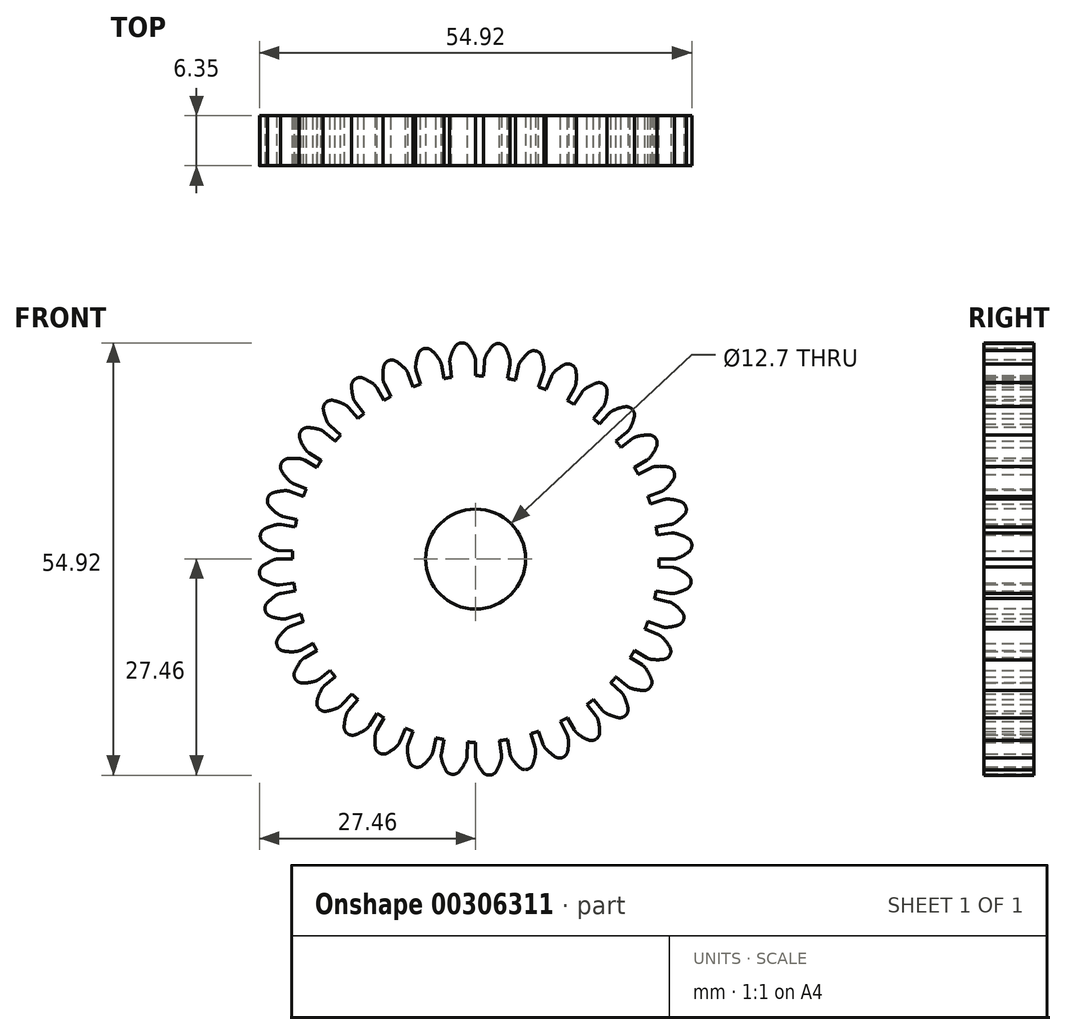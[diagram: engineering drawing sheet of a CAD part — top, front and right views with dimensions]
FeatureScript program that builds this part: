
annotation { "Feature Type Name" : "Feature", "Feature Type Description" : "" }
export const myFeature = defineFeature(function(context is Context, id is Id, definition is map)
    precondition{}
    {
        {
            var Q0;
            Q0=qCreatedBy(makeId("Front.planeOp"),FACE);
            var sketch = newSketch(context, id + "F0", { "sketchPlane" : qUnion([Q0])});
            skCircle(sketch, "E0", {"center": v(0, 0) * mm, "radius": 23.28 * mm});
            skArc(sketch, "E1.trimOffspring", {"start": v(-0.13, 25.73) * mm, "mid": v(-0.47, 26.41) * mm, "end": v(-0.9, 27.06) * mm});
            skLineSegment(sketch, "E2", {"start": v(0, 25.1) * mm, "end": v(0, 23.28) * mm});
            skLineSegment(sketch, "E3", {"start": v(-1.78, 27.46) * mm, "end": v(-1.8, 27.46) * mm});
            skArc(sketch, "E4.MirrorCS", {"start": v(-3.23, 25.52) * mm, "mid": v(-2.98, 26.25) * mm, "end": v(-2.64, 26.94) * mm});
            skLineSegment(sketch, "E5.MirrorCS", {"start": v(-3.28, 24.88) * mm, "end": v(-3.04, 23.08) * mm});
            skLineSegment(sketch, "E6.MirrorCS", {"start": v(-1.82, 27.46) * mm, "end": v(-1.8, 27.46) * mm});
            skPoint(sketch, "E7.visualSharp", {"position": v(-1.26, 27.5) * mm});
            skArc(sketch, "E7.filletArc", {"start": v(-0.9, 27.06) * mm, "mid": v(-1.29, 27.37) * mm, "end": v(-1.78, 27.46) * mm});
            skPoint(sketch, "E8.visualSharp", {"position": v(-2.34, 27.42) * mm});
            skArc(sketch, "E8.filletArc", {"start": v(-1.82, 27.46) * mm, "mid": v(-2.3, 27.3) * mm, "end": v(-2.64, 26.94) * mm});
            skPoint(sketch, "E9.visualSharp", {"position": v(-3.32, 25.18) * mm});
            skArc(sketch, "E9.filletArc", {"start": v(-3.27, 25.38) * mm, "mid": v(-3.3, 25.2) * mm, "end": v(-3.3, 25) * mm});
            skArc(sketch, "E10.filletArc", {"start": v(-3.23, 25.52) * mm, "mid": v(-3.29, 25.2) * mm, "end": v(-3.28, 24.88) * mm});
            skPoint(sketch, "E11.visualSharp", {"position": v(0, 25.4) * mm});
            skArc(sketch, "E11.filletArc", {"start": v(0, 25.1) * mm, "mid": v(-0.03, 25.42) * mm, "end": v(-0.13, 25.73) * mm});
            skArc(sketch, "E12.1.0", {"start": v(-5.59, 26.49) * mm, "mid": v(-6.02, 26.73) * mm, "end": v(-6.52, 26.73) * mm});
            skArc(sketch, "E12.1.1", {"start": v(-6.56, 26.72) * mm, "mid": v(-7, 26.49) * mm, "end": v(-7.28, 26.08) * mm});
            skArc(sketch, "E12.1.2", {"start": v(-7.61, 24.57) * mm, "mid": v(-7.5, 25.34) * mm, "end": v(-7.28, 26.08) * mm});
            skArc(sketch, "E12.1.3", {"start": v(-7.61, 24.57) * mm, "mid": v(-7.61, 24.25) * mm, "end": v(-7.55, 23.94) * mm});
            skLineSegment(sketch, "E12.1.4", {"start": v(-7.55, 23.94) * mm, "end": v(-7, 22.2) * mm});
            skLineSegment(sketch, "E12.1.5", {"start": v(-4.36, 24.72) * mm, "end": v(-4.04, 22.93) * mm});
            skArc(sketch, "E12.1.6", {"start": v(-4.36, 24.72) * mm, "mid": v(-4.45, 25.03) * mm, "end": v(-4.6, 25.31) * mm});
            skArc(sketch, "E12.1.7", {"start": v(-4.6, 25.31) * mm, "mid": v(-5.05, 25.93) * mm, "end": v(-5.59, 26.49) * mm});
            skArc(sketch, "E12.2.0", {"start": v(-10.1, 25.12) * mm, "mid": v(-10.57, 25.28) * mm, "end": v(-11.06, 25.2) * mm});
            skArc(sketch, "E12.2.1", {"start": v(-11.1, 25.18) * mm, "mid": v(-11.5, 24.87) * mm, "end": v(-11.7, 24.42) * mm});
            skArc(sketch, "E12.2.2", {"start": v(-11.76, 22.88) * mm, "mid": v(-11.78, 23.65) * mm, "end": v(-11.7, 24.42) * mm});
            skArc(sketch, "E12.2.3", {"start": v(-11.76, 22.88) * mm, "mid": v(-11.7, 22.56) * mm, "end": v(-11.59, 22.26) * mm});
            skLineSegment(sketch, "E12.2.4", {"start": v(-11.59, 22.26) * mm, "end": v(-10.75, 20.65) * mm});
            skLineSegment(sketch, "E12.2.5", {"start": v(-8.58, 23.58) * mm, "end": v(-7.96, 21.88) * mm});
            skArc(sketch, "E12.2.6", {"start": v(-8.58, 23.58) * mm, "mid": v(-8.72, 23.87) * mm, "end": v(-8.92, 24.13) * mm});
            skArc(sketch, "E12.2.7", {"start": v(-8.92, 24.13) * mm, "mid": v(-9.48, 24.66) * mm, "end": v(-10.1, 25.12) * mm});
            skArc(sketch, "E13.1.3.0", {"start": v(-14.3, 22.98) * mm, "mid": v(-14.8, 23.06) * mm, "end": v(-15.27, 22.9) * mm});
            skArc(sketch, "E13.4.3.0", {"start": v(-15.3, 22.87) * mm, "mid": v(-15.64, 22.5) * mm, "end": v(-15.76, 22.01) * mm});
            skArc(sketch, "E13.8.3.0", {"start": v(-15.56, 20.49) * mm, "mid": v(-15.7, 21.25) * mm, "end": v(-15.76, 22.01) * mm});
            skArc(sketch, "E13.12.3.0", {"start": v(-15.56, 20.49) * mm, "mid": v(-15.45, 20.19) * mm, "end": v(-15.28, 19.91) * mm});
            skLineSegment(sketch, "E13.16.3.0", {"start": v(-15.28, 19.91) * mm, "end": v(-14.17, 18.47) * mm});
            skLineSegment(sketch, "E13.19.3.0", {"start": v(-12.55, 21.73) * mm, "end": v(-11.64, 20.16) * mm});
            skArc(sketch, "E13.22.3.0", {"start": v(-12.55, 21.73) * mm, "mid": v(-12.74, 22) * mm, "end": v(-12.97, 22.21) * mm});
            skArc(sketch, "E13.26.3.0", {"start": v(-12.97, 22.21) * mm, "mid": v(-13.62, 22.64) * mm, "end": v(-14.3, 22.98) * mm});
            skArc(sketch, "E13.1.4.0", {"start": v(-18.08, 20.15) * mm, "mid": v(-18.58, 20.14) * mm, "end": v(-19.01, 19.9) * mm});
            skArc(sketch, "E13.4.4.0", {"start": v(-19.04, 19.86) * mm, "mid": v(-19.3, 19.44) * mm, "end": v(-19.34, 18.94) * mm});
            skArc(sketch, "E13.8.4.0", {"start": v(-18.88, 17.48) * mm, "mid": v(-19.15, 18.2) * mm, "end": v(-19.34, 18.94) * mm});
            skArc(sketch, "E13.12.4.0", {"start": v(-18.88, 17.48) * mm, "mid": v(-18.72, 17.2) * mm, "end": v(-18.5, 16.96) * mm});
            skLineSegment(sketch, "E13.16.4.0", {"start": v(-18.5, 16.96) * mm, "end": v(-17.16, 15.73) * mm});
            skLineSegment(sketch, "E13.19.4.0", {"start": v(-16.13, 19.23) * mm, "end": v(-14.96, 17.83) * mm});
            skArc(sketch, "E13.22.4.0", {"start": v(-16.13, 19.23) * mm, "mid": v(-16.36, 19.45) * mm, "end": v(-16.64, 19.62) * mm});
            skArc(sketch, "E13.26.4.0", {"start": v(-16.64, 19.62) * mm, "mid": v(-17.34, 19.93) * mm, "end": v(-18.08, 20.15) * mm});
            skArc(sketch, "E13.1.5.0", {"start": v(-21.3, 16.7) * mm, "mid": v(-21.8, 16.6) * mm, "end": v(-22.18, 16.29) * mm});
            skArc(sketch, "E13.4.5.0", {"start": v(-22.2, 16.25) * mm, "mid": v(-22.39, 15.8) * mm, "end": v(-22.34, 15.3) * mm});
            skArc(sketch, "E13.8.5.0", {"start": v(-21.63, 13.93) * mm, "mid": v(-22.02, 14.6) * mm, "end": v(-22.34, 15.3) * mm});
            skArc(sketch, "E13.12.5.0", {"start": v(-21.63, 13.93) * mm, "mid": v(-21.42, 13.68) * mm, "end": v(-21.17, 13.48) * mm});
            skLineSegment(sketch, "E13.16.5.0", {"start": v(-21.17, 13.48) * mm, "end": v(-19.63, 12.5) * mm});
            skLineSegment(sketch, "E13.19.5.0", {"start": v(-19.23, 16.13) * mm, "end": v(-17.83, 14.96) * mm});
            skArc(sketch, "E13.22.5.0", {"start": v(-19.23, 16.13) * mm, "mid": v(-19.5, 16.31) * mm, "end": v(-19.8, 16.44) * mm});
            skArc(sketch, "E13.26.5.0", {"start": v(-19.8, 16.44) * mm, "mid": v(-20.54, 16.62) * mm, "end": v(-21.3, 16.7) * mm});
            skArc(sketch, "E13.1.6.0", {"start": v(-23.88, 12.75) * mm, "mid": v(-24.35, 12.57) * mm, "end": v(-24.67, 12.19) * mm});
            skArc(sketch, "E13.4.6.0", {"start": v(-24.69, 12.15) * mm, "mid": v(-24.8, 11.66) * mm, "end": v(-24.65, 11.19) * mm});
            skArc(sketch, "E13.8.6.0", {"start": v(-23.72, 9.96) * mm, "mid": v(-24.22, 10.55) * mm, "end": v(-24.65, 11.19) * mm});
            skArc(sketch, "E13.12.6.0", {"start": v(-23.72, 9.96) * mm, "mid": v(-23.47, 9.76) * mm, "end": v(-23.19, 9.6) * mm});
            skLineSegment(sketch, "E13.16.6.0", {"start": v(-23.19, 9.6) * mm, "end": v(-21.5, 8.9) * mm});
            skLineSegment(sketch, "E13.19.6.0", {"start": v(-21.73, 12.55) * mm, "end": v(-20.16, 11.64) * mm});
            skArc(sketch, "E13.22.6.0", {"start": v(-21.73, 12.55) * mm, "mid": v(-22.03, 12.68) * mm, "end": v(-22.34, 12.75) * mm});
            skArc(sketch, "E13.26.6.0", {"start": v(-22.34, 12.75) * mm, "mid": v(-23.11, 12.8) * mm, "end": v(-23.88, 12.75) * mm});
            skArc(sketch, "E13.1.7.0", {"start": v(-25.73, 8.4) * mm, "mid": v(-26.16, 8.15) * mm, "end": v(-26.41, 7.72) * mm});
            skArc(sketch, "E13.4.7.0", {"start": v(-26.42, 7.68) * mm, "mid": v(-26.44, 7.18) * mm, "end": v(-26.22, 6.74) * mm});
            skArc(sketch, "E13.8.7.0", {"start": v(-25.09, 5.7) * mm, "mid": v(-25.69, 6.18) * mm, "end": v(-26.22, 6.74) * mm});
            skArc(sketch, "E13.12.7.0", {"start": v(-25.09, 5.7) * mm, "mid": v(-24.8, 5.53) * mm, "end": v(-24.5, 5.43) * mm});
            skLineSegment(sketch, "E13.16.7.0", {"start": v(-24.5, 5.43) * mm, "end": v(-22.73, 5.04) * mm});
            skLineSegment(sketch, "E13.19.7.0", {"start": v(-23.58, 8.58) * mm, "end": v(-21.88, 7.96) * mm});
            skArc(sketch, "E13.22.7.0", {"start": v(-23.58, 8.58) * mm, "mid": v(-23.9, 8.66) * mm, "end": v(-24.22, 8.68) * mm});
            skArc(sketch, "E13.26.7.0", {"start": v(-24.22, 8.68) * mm, "mid": v(-24.98, 8.59) * mm, "end": v(-25.73, 8.4) * mm});
            skArc(sketch, "E13.1.8.0", {"start": v(-26.8, 3.81) * mm, "mid": v(-27.18, 3.48) * mm, "end": v(-27.35, 3.02) * mm});
            skArc(sketch, "E13.4.8.0", {"start": v(-27.35, 2.97) * mm, "mid": v(-27.29, 2.48) * mm, "end": v(-27, 2.08) * mm});
            skArc(sketch, "E13.8.8.0", {"start": v(-25.7, 1.25) * mm, "mid": v(-26.37, 1.63) * mm, "end": v(-27, 2.08) * mm});
            skArc(sketch, "E13.12.8.0", {"start": v(-25.7, 1.25) * mm, "mid": v(-25.4, 1.14) * mm, "end": v(-25.07, 1.1) * mm});
            skLineSegment(sketch, "E13.16.8.0", {"start": v(-25.07, 1.1) * mm, "end": v(-23.26, 1.02) * mm});
            skLineSegment(sketch, "E13.19.8.0", {"start": v(-24.72, 4.36) * mm, "end": v(-22.93, 4.04) * mm});
            skArc(sketch, "E13.22.8.0", {"start": v(-24.72, 4.36) * mm, "mid": v(-25.04, 4.38) * mm, "end": v(-25.36, 4.34) * mm});
            skArc(sketch, "E13.26.8.0", {"start": v(-25.36, 4.34) * mm, "mid": v(-26.1, 4.12) * mm, "end": v(-26.8, 3.81) * mm});
            skArc(sketch, "E13.1.9.0", {"start": v(-27.06, -0.9) * mm, "mid": v(-27.37, -1.29) * mm, "end": v(-27.46, -1.78) * mm});
            skArc(sketch, "E13.4.9.0", {"start": v(-27.46, -1.82) * mm, "mid": v(-27.3, -2.3) * mm, "end": v(-26.94, -2.64) * mm});
            skArc(sketch, "E13.8.9.0", {"start": v(-25.52, -3.23) * mm, "mid": v(-26.25, -2.98) * mm, "end": v(-26.94, -2.64) * mm});
            skArc(sketch, "E13.12.9.0", {"start": v(-25.52, -3.23) * mm, "mid": v(-25.2, -3.29) * mm, "end": v(-24.88, -3.28) * mm});
            skLineSegment(sketch, "E13.16.9.0", {"start": v(-24.88, -3.28) * mm, "end": v(-23.08, -3.04) * mm});
            skLineSegment(sketch, "E13.19.9.0", {"start": v(-25.1, 0) * mm, "end": v(-23.28, 0) * mm});
            skArc(sketch, "E13.22.9.0", {"start": v(-25.1, 0) * mm, "mid": v(-25.42, -0.03) * mm, "end": v(-25.73, -0.13) * mm});
            skArc(sketch, "E13.26.9.0", {"start": v(-25.73, -0.13) * mm, "mid": v(-26.41, -0.47) * mm, "end": v(-27.06, -0.9) * mm});
            skArc(sketch, "E13.1.10.0", {"start": v(-26.49, -5.59) * mm, "mid": v(-26.73, -6.02) * mm, "end": v(-26.73, -6.52) * mm});
            skArc(sketch, "E13.4.10.0", {"start": v(-26.72, -6.56) * mm, "mid": v(-26.49, -7) * mm, "end": v(-26.08, -7.28) * mm});
            skArc(sketch, "E13.8.10.0", {"start": v(-24.57, -7.61) * mm, "mid": v(-25.34, -7.5) * mm, "end": v(-26.08, -7.28) * mm});
            skArc(sketch, "E13.12.10.0", {"start": v(-24.57, -7.61) * mm, "mid": v(-24.25, -7.61) * mm, "end": v(-23.94, -7.55) * mm});
            skLineSegment(sketch, "E13.16.10.0", {"start": v(-23.94, -7.55) * mm, "end": v(-22.2, -7) * mm});
            skLineSegment(sketch, "E13.19.10.0", {"start": v(-24.72, -4.36) * mm, "end": v(-22.93, -4.04) * mm});
            skArc(sketch, "E13.22.10.0", {"start": v(-24.72, -4.36) * mm, "mid": v(-25.03, -4.45) * mm, "end": v(-25.31, -4.6) * mm});
            skArc(sketch, "E13.26.10.0", {"start": v(-25.31, -4.6) * mm, "mid": v(-25.93, -5.05) * mm, "end": v(-26.49, -5.59) * mm});
            skArc(sketch, "E13.1.11.0", {"start": v(-25.12, -10.1) * mm, "mid": v(-25.28, -10.57) * mm, "end": v(-25.2, -11.06) * mm});
            skArc(sketch, "E13.4.11.0", {"start": v(-25.18, -11.1) * mm, "mid": v(-24.87, -11.5) * mm, "end": v(-24.42, -11.7) * mm});
            skArc(sketch, "E13.8.11.0", {"start": v(-22.88, -11.76) * mm, "mid": v(-23.65, -11.78) * mm, "end": v(-24.42, -11.7) * mm});
            skArc(sketch, "E13.12.11.0", {"start": v(-22.88, -11.76) * mm, "mid": v(-22.56, -11.7) * mm, "end": v(-22.26, -11.59) * mm});
            skLineSegment(sketch, "E13.16.11.0", {"start": v(-22.26, -11.59) * mm, "end": v(-20.65, -10.75) * mm});
            skLineSegment(sketch, "E13.19.11.0", {"start": v(-23.58, -8.58) * mm, "end": v(-21.88, -7.96) * mm});
            skArc(sketch, "E13.22.11.0", {"start": v(-23.58, -8.58) * mm, "mid": v(-23.87, -8.72) * mm, "end": v(-24.13, -8.92) * mm});
            skArc(sketch, "E13.26.11.0", {"start": v(-24.13, -8.92) * mm, "mid": v(-24.66, -9.48) * mm, "end": v(-25.12, -10.1) * mm});
            skArc(sketch, "E13.1.12.0", {"start": v(-22.98, -14.3) * mm, "mid": v(-23.06, -14.8) * mm, "end": v(-22.9, -15.27) * mm});
            skArc(sketch, "E13.4.12.0", {"start": v(-22.87, -15.3) * mm, "mid": v(-22.5, -15.64) * mm, "end": v(-22.01, -15.76) * mm});
            skArc(sketch, "E13.8.12.0", {"start": v(-20.49, -15.56) * mm, "mid": v(-21.25, -15.7) * mm, "end": v(-22.01, -15.76) * mm});
            skArc(sketch, "E13.12.12.0", {"start": v(-20.49, -15.56) * mm, "mid": v(-20.19, -15.45) * mm, "end": v(-19.91, -15.28) * mm});
            skLineSegment(sketch, "E13.16.12.0", {"start": v(-19.91, -15.28) * mm, "end": v(-18.47, -14.17) * mm});
            skLineSegment(sketch, "E13.19.12.0", {"start": v(-21.73, -12.55) * mm, "end": v(-20.16, -11.64) * mm});
            skArc(sketch, "E13.22.12.0", {"start": v(-21.73, -12.55) * mm, "mid": v(-22, -12.74) * mm, "end": v(-22.21, -12.97) * mm});
            skArc(sketch, "E13.26.12.0", {"start": v(-22.21, -12.97) * mm, "mid": v(-22.64, -13.62) * mm, "end": v(-22.98, -14.3) * mm});
            skArc(sketch, "E13.1.13.0", {"start": v(-20.15, -18.08) * mm, "mid": v(-20.14, -18.58) * mm, "end": v(-19.9, -19.01) * mm});
            skArc(sketch, "E13.4.13.0", {"start": v(-19.86, -19.04) * mm, "mid": v(-19.44, -19.3) * mm, "end": v(-18.94, -19.34) * mm});
            skArc(sketch, "E13.8.13.0", {"start": v(-17.48, -18.88) * mm, "mid": v(-18.2, -19.15) * mm, "end": v(-18.94, -19.34) * mm});
            skArc(sketch, "E13.12.13.0", {"start": v(-17.48, -18.88) * mm, "mid": v(-17.2, -18.72) * mm, "end": v(-16.96, -18.5) * mm});
            skLineSegment(sketch, "E13.16.13.0", {"start": v(-16.96, -18.5) * mm, "end": v(-15.73, -17.16) * mm});
            skLineSegment(sketch, "E13.19.13.0", {"start": v(-19.23, -16.13) * mm, "end": v(-17.83, -14.96) * mm});
            skArc(sketch, "E13.22.13.0", {"start": v(-19.23, -16.13) * mm, "mid": v(-19.45, -16.36) * mm, "end": v(-19.62, -16.64) * mm});
            skArc(sketch, "E13.26.13.0", {"start": v(-19.62, -16.64) * mm, "mid": v(-19.93, -17.34) * mm, "end": v(-20.15, -18.08) * mm});
            skArc(sketch, "E13.1.14.0", {"start": v(-16.7, -21.3) * mm, "mid": v(-16.6, -21.8) * mm, "end": v(-16.29, -22.18) * mm});
            skArc(sketch, "E13.4.14.0", {"start": v(-16.25, -22.2) * mm, "mid": v(-15.8, -22.39) * mm, "end": v(-15.3, -22.34) * mm});
            skArc(sketch, "E13.8.14.0", {"start": v(-13.93, -21.63) * mm, "mid": v(-14.6, -22.02) * mm, "end": v(-15.3, -22.34) * mm});
            skArc(sketch, "E13.12.14.0", {"start": v(-13.93, -21.63) * mm, "mid": v(-13.68, -21.42) * mm, "end": v(-13.48, -21.17) * mm});
            skLineSegment(sketch, "E13.16.14.0", {"start": v(-13.48, -21.17) * mm, "end": v(-12.5, -19.63) * mm});
            skLineSegment(sketch, "E13.19.14.0", {"start": v(-16.13, -19.23) * mm, "end": v(-14.96, -17.83) * mm});
            skArc(sketch, "E13.22.14.0", {"start": v(-16.13, -19.23) * mm, "mid": v(-16.31, -19.5) * mm, "end": v(-16.44, -19.8) * mm});
            skArc(sketch, "E13.26.14.0", {"start": v(-16.44, -19.8) * mm, "mid": v(-16.62, -20.54) * mm, "end": v(-16.7, -21.3) * mm});
            skArc(sketch, "E13.1.15.0", {"start": v(-12.75, -23.88) * mm, "mid": v(-12.57, -24.35) * mm, "end": v(-12.19, -24.67) * mm});
            skArc(sketch, "E13.4.15.0", {"start": v(-12.15, -24.69) * mm, "mid": v(-11.66, -24.8) * mm, "end": v(-11.19, -24.65) * mm});
            skArc(sketch, "E13.8.15.0", {"start": v(-9.96, -23.72) * mm, "mid": v(-10.55, -24.22) * mm, "end": v(-11.19, -24.65) * mm});
            skArc(sketch, "E13.12.15.0", {"start": v(-9.96, -23.72) * mm, "mid": v(-9.76, -23.47) * mm, "end": v(-9.6, -23.19) * mm});
            skLineSegment(sketch, "E13.16.15.0", {"start": v(-9.6, -23.19) * mm, "end": v(-8.9, -21.5) * mm});
            skLineSegment(sketch, "E13.19.15.0", {"start": v(-12.55, -21.73) * mm, "end": v(-11.64, -20.16) * mm});
            skArc(sketch, "E13.22.15.0", {"start": v(-12.55, -21.73) * mm, "mid": v(-12.68, -22.03) * mm, "end": v(-12.75, -22.34) * mm});
            skArc(sketch, "E13.26.15.0", {"start": v(-12.75, -22.34) * mm, "mid": v(-12.8, -23.11) * mm, "end": v(-12.75, -23.88) * mm});
            skArc(sketch, "E13.1.16.0", {"start": v(-8.4, -25.73) * mm, "mid": v(-8.15, -26.16) * mm, "end": v(-7.72, -26.41) * mm});
            skArc(sketch, "E13.4.16.0", {"start": v(-7.68, -26.42) * mm, "mid": v(-7.18, -26.44) * mm, "end": v(-6.74, -26.22) * mm});
            skArc(sketch, "E13.8.16.0", {"start": v(-5.7, -25.09) * mm, "mid": v(-6.18, -25.69) * mm, "end": v(-6.74, -26.22) * mm});
            skArc(sketch, "E13.12.16.0", {"start": v(-5.7, -25.09) * mm, "mid": v(-5.53, -24.8) * mm, "end": v(-5.43, -24.5) * mm});
            skLineSegment(sketch, "E13.16.16.0", {"start": v(-5.43, -24.5) * mm, "end": v(-5.04, -22.73) * mm});
            skLineSegment(sketch, "E13.19.16.0", {"start": v(-8.58, -23.58) * mm, "end": v(-7.96, -21.88) * mm});
            skArc(sketch, "E13.22.16.0", {"start": v(-8.58, -23.58) * mm, "mid": v(-8.66, -23.9) * mm, "end": v(-8.68, -24.22) * mm});
            skArc(sketch, "E13.26.16.0", {"start": v(-8.68, -24.22) * mm, "mid": v(-8.59, -24.98) * mm, "end": v(-8.4, -25.73) * mm});
            skArc(sketch, "E13.1.17.0", {"start": v(-3.81, -26.8) * mm, "mid": v(-3.48, -27.18) * mm, "end": v(-3.02, -27.35) * mm});
            skArc(sketch, "E13.4.17.0", {"start": v(-2.97, -27.35) * mm, "mid": v(-2.48, -27.29) * mm, "end": v(-2.08, -27) * mm});
            skArc(sketch, "E13.8.17.0", {"start": v(-1.25, -25.7) * mm, "mid": v(-1.63, -26.37) * mm, "end": v(-2.08, -27) * mm});
            skArc(sketch, "E13.12.17.0", {"start": v(-1.25, -25.7) * mm, "mid": v(-1.14, -25.4) * mm, "end": v(-1.1, -25.07) * mm});
            skLineSegment(sketch, "E13.16.17.0", {"start": v(-1.1, -25.07) * mm, "end": v(-1.02, -23.26) * mm});
            skLineSegment(sketch, "E13.19.17.0", {"start": v(-4.36, -24.72) * mm, "end": v(-4.04, -22.93) * mm});
            skArc(sketch, "E13.22.17.0", {"start": v(-4.36, -24.72) * mm, "mid": v(-4.38, -25.04) * mm, "end": v(-4.34, -25.36) * mm});
            skArc(sketch, "E13.26.17.0", {"start": v(-4.34, -25.36) * mm, "mid": v(-4.12, -26.1) * mm, "end": v(-3.81, -26.8) * mm});
            skArc(sketch, "E13.1.18.0", {"start": v(0.9, -27.06) * mm, "mid": v(1.29, -27.37) * mm, "end": v(1.78, -27.46) * mm});
            skArc(sketch, "E13.4.18.0", {"start": v(1.82, -27.46) * mm, "mid": v(2.3, -27.3) * mm, "end": v(2.64, -26.94) * mm});
            skArc(sketch, "E13.8.18.0", {"start": v(3.23, -25.52) * mm, "mid": v(2.98, -26.25) * mm, "end": v(2.64, -26.94) * mm});
            skArc(sketch, "E13.12.18.0", {"start": v(3.23, -25.52) * mm, "mid": v(3.29, -25.2) * mm, "end": v(3.28, -24.88) * mm});
            skLineSegment(sketch, "E13.16.18.0", {"start": v(3.28, -24.88) * mm, "end": v(3.04, -23.08) * mm});
            skLineSegment(sketch, "E13.19.18.0", {"start": v(0, -25.1) * mm, "end": v(0, -23.28) * mm});
            skArc(sketch, "E13.22.18.0", {"start": v(0, -25.1) * mm, "mid": v(0.03, -25.42) * mm, "end": v(0.13, -25.73) * mm});
            skArc(sketch, "E13.26.18.0", {"start": v(0.13, -25.73) * mm, "mid": v(0.47, -26.41) * mm, "end": v(0.9, -27.06) * mm});
            skArc(sketch, "E13.1.19.0", {"start": v(5.59, -26.49) * mm, "mid": v(6.02, -26.73) * mm, "end": v(6.52, -26.73) * mm});
            skArc(sketch, "E13.4.19.0", {"start": v(6.56, -26.72) * mm, "mid": v(7, -26.49) * mm, "end": v(7.28, -26.08) * mm});
            skArc(sketch, "E13.8.19.0", {"start": v(7.61, -24.57) * mm, "mid": v(7.5, -25.34) * mm, "end": v(7.28, -26.08) * mm});
            skArc(sketch, "E13.12.19.0", {"start": v(7.61, -24.57) * mm, "mid": v(7.61, -24.25) * mm, "end": v(7.55, -23.94) * mm});
            skLineSegment(sketch, "E13.16.19.0", {"start": v(7.55, -23.94) * mm, "end": v(7, -22.2) * mm});
            skLineSegment(sketch, "E13.19.19.0", {"start": v(4.36, -24.72) * mm, "end": v(4.04, -22.93) * mm});
            skArc(sketch, "E13.22.19.0", {"start": v(4.36, -24.72) * mm, "mid": v(4.45, -25.03) * mm, "end": v(4.6, -25.31) * mm});
            skArc(sketch, "E13.26.19.0", {"start": v(4.6, -25.31) * mm, "mid": v(5.05, -25.93) * mm, "end": v(5.59, -26.49) * mm});
            skArc(sketch, "E13.1.20.0", {"start": v(10.1, -25.12) * mm, "mid": v(10.57, -25.28) * mm, "end": v(11.06, -25.2) * mm});
            skArc(sketch, "E13.4.20.0", {"start": v(11.1, -25.18) * mm, "mid": v(11.5, -24.87) * mm, "end": v(11.7, -24.42) * mm});
            skArc(sketch, "E13.8.20.0", {"start": v(11.76, -22.88) * mm, "mid": v(11.78, -23.65) * mm, "end": v(11.7, -24.42) * mm});
            skArc(sketch, "E13.12.20.0", {"start": v(11.76, -22.88) * mm, "mid": v(11.7, -22.56) * mm, "end": v(11.59, -22.26) * mm});
            skLineSegment(sketch, "E13.16.20.0", {"start": v(11.59, -22.26) * mm, "end": v(10.75, -20.65) * mm});
            skLineSegment(sketch, "E13.19.20.0", {"start": v(8.58, -23.58) * mm, "end": v(7.96, -21.88) * mm});
            skArc(sketch, "E13.22.20.0", {"start": v(8.58, -23.58) * mm, "mid": v(8.72, -23.87) * mm, "end": v(8.92, -24.13) * mm});
            skArc(sketch, "E13.26.20.0", {"start": v(8.92, -24.13) * mm, "mid": v(9.48, -24.66) * mm, "end": v(10.1, -25.12) * mm});
            skArc(sketch, "E13.1.21.0", {"start": v(14.3, -22.98) * mm, "mid": v(14.8, -23.06) * mm, "end": v(15.27, -22.9) * mm});
            skArc(sketch, "E13.4.21.0", {"start": v(15.3, -22.87) * mm, "mid": v(15.64, -22.5) * mm, "end": v(15.76, -22.01) * mm});
            skArc(sketch, "E13.8.21.0", {"start": v(15.56, -20.49) * mm, "mid": v(15.7, -21.25) * mm, "end": v(15.76, -22.01) * mm});
            skArc(sketch, "E13.12.21.0", {"start": v(15.56, -20.49) * mm, "mid": v(15.45, -20.19) * mm, "end": v(15.28, -19.91) * mm});
            skLineSegment(sketch, "E13.16.21.0", {"start": v(15.28, -19.91) * mm, "end": v(14.17, -18.47) * mm});
            skLineSegment(sketch, "E13.19.21.0", {"start": v(12.55, -21.73) * mm, "end": v(11.64, -20.16) * mm});
            skArc(sketch, "E13.22.21.0", {"start": v(12.55, -21.73) * mm, "mid": v(12.74, -22) * mm, "end": v(12.97, -22.21) * mm});
            skArc(sketch, "E13.26.21.0", {"start": v(12.97, -22.21) * mm, "mid": v(13.62, -22.64) * mm, "end": v(14.3, -22.98) * mm});
            skArc(sketch, "E13.1.22.0", {"start": v(18.08, -20.15) * mm, "mid": v(18.58, -20.14) * mm, "end": v(19.01, -19.9) * mm});
            skArc(sketch, "E13.4.22.0", {"start": v(19.04, -19.86) * mm, "mid": v(19.3, -19.44) * mm, "end": v(19.34, -18.94) * mm});
            skArc(sketch, "E13.8.22.0", {"start": v(18.88, -17.48) * mm, "mid": v(19.15, -18.2) * mm, "end": v(19.34, -18.94) * mm});
            skArc(sketch, "E13.12.22.0", {"start": v(18.88, -17.48) * mm, "mid": v(18.72, -17.2) * mm, "end": v(18.5, -16.96) * mm});
            skLineSegment(sketch, "E13.16.22.0", {"start": v(18.5, -16.96) * mm, "end": v(17.16, -15.73) * mm});
            skLineSegment(sketch, "E13.19.22.0", {"start": v(16.13, -19.23) * mm, "end": v(14.96, -17.83) * mm});
            skArc(sketch, "E13.22.22.0", {"start": v(16.13, -19.23) * mm, "mid": v(16.36, -19.45) * mm, "end": v(16.64, -19.62) * mm});
            skArc(sketch, "E13.26.22.0", {"start": v(16.64, -19.62) * mm, "mid": v(17.34, -19.93) * mm, "end": v(18.08, -20.15) * mm});
            skArc(sketch, "E13.1.23.0", {"start": v(21.3, -16.7) * mm, "mid": v(21.8, -16.6) * mm, "end": v(22.18, -16.29) * mm});
            skArc(sketch, "E13.4.23.0", {"start": v(22.2, -16.25) * mm, "mid": v(22.39, -15.8) * mm, "end": v(22.34, -15.3) * mm});
            skArc(sketch, "E13.8.23.0", {"start": v(21.63, -13.93) * mm, "mid": v(22.02, -14.6) * mm, "end": v(22.34, -15.3) * mm});
            skArc(sketch, "E13.12.23.0", {"start": v(21.63, -13.93) * mm, "mid": v(21.42, -13.68) * mm, "end": v(21.17, -13.48) * mm});
            skLineSegment(sketch, "E13.16.23.0", {"start": v(21.17, -13.48) * mm, "end": v(19.63, -12.5) * mm});
            skLineSegment(sketch, "E13.19.23.0", {"start": v(19.23, -16.13) * mm, "end": v(17.83, -14.96) * mm});
            skArc(sketch, "E13.22.23.0", {"start": v(19.23, -16.13) * mm, "mid": v(19.5, -16.31) * mm, "end": v(19.8, -16.44) * mm});
            skArc(sketch, "E13.26.23.0", {"start": v(19.8, -16.44) * mm, "mid": v(20.54, -16.62) * mm, "end": v(21.3, -16.7) * mm});
            skArc(sketch, "E13.1.24.0", {"start": v(23.88, -12.75) * mm, "mid": v(24.35, -12.57) * mm, "end": v(24.67, -12.19) * mm});
            skArc(sketch, "E13.4.24.0", {"start": v(24.69, -12.15) * mm, "mid": v(24.8, -11.66) * mm, "end": v(24.65, -11.19) * mm});
            skArc(sketch, "E13.8.24.0", {"start": v(23.72, -9.96) * mm, "mid": v(24.22, -10.55) * mm, "end": v(24.65, -11.19) * mm});
            skArc(sketch, "E13.12.24.0", {"start": v(23.72, -9.96) * mm, "mid": v(23.47, -9.76) * mm, "end": v(23.19, -9.6) * mm});
            skLineSegment(sketch, "E13.16.24.0", {"start": v(23.19, -9.6) * mm, "end": v(21.5, -8.9) * mm});
            skLineSegment(sketch, "E13.19.24.0", {"start": v(21.73, -12.55) * mm, "end": v(20.16, -11.64) * mm});
            skArc(sketch, "E13.22.24.0", {"start": v(21.73, -12.55) * mm, "mid": v(22.03, -12.68) * mm, "end": v(22.34, -12.75) * mm});
            skArc(sketch, "E13.26.24.0", {"start": v(22.34, -12.75) * mm, "mid": v(23.11, -12.8) * mm, "end": v(23.88, -12.75) * mm});
            skArc(sketch, "E13.1.25.0", {"start": v(25.73, -8.4) * mm, "mid": v(26.16, -8.15) * mm, "end": v(26.41, -7.72) * mm});
            skArc(sketch, "E13.4.25.0", {"start": v(26.42, -7.68) * mm, "mid": v(26.44, -7.18) * mm, "end": v(26.22, -6.74) * mm});
            skArc(sketch, "E13.8.25.0", {"start": v(25.09, -5.7) * mm, "mid": v(25.69, -6.18) * mm, "end": v(26.22, -6.74) * mm});
            skArc(sketch, "E13.12.25.0", {"start": v(25.09, -5.7) * mm, "mid": v(24.8, -5.53) * mm, "end": v(24.5, -5.43) * mm});
            skLineSegment(sketch, "E13.16.25.0", {"start": v(24.5, -5.43) * mm, "end": v(22.73, -5.04) * mm});
            skLineSegment(sketch, "E13.19.25.0", {"start": v(23.58, -8.58) * mm, "end": v(21.88, -7.96) * mm});
            skArc(sketch, "E13.22.25.0", {"start": v(23.58, -8.58) * mm, "mid": v(23.9, -8.66) * mm, "end": v(24.22, -8.68) * mm});
            skArc(sketch, "E13.26.25.0", {"start": v(24.22, -8.68) * mm, "mid": v(24.98, -8.59) * mm, "end": v(25.73, -8.4) * mm});
            skArc(sketch, "E13.1.26.0", {"start": v(26.8, -3.81) * mm, "mid": v(27.18, -3.48) * mm, "end": v(27.35, -3.02) * mm});
            skArc(sketch, "E13.4.26.0", {"start": v(27.35, -2.97) * mm, "mid": v(27.29, -2.48) * mm, "end": v(27, -2.08) * mm});
            skArc(sketch, "E13.8.26.0", {"start": v(25.7, -1.25) * mm, "mid": v(26.37, -1.63) * mm, "end": v(27, -2.08) * mm});
            skArc(sketch, "E13.12.26.0", {"start": v(25.7, -1.25) * mm, "mid": v(25.4, -1.14) * mm, "end": v(25.07, -1.1) * mm});
            skLineSegment(sketch, "E13.16.26.0", {"start": v(25.07, -1.1) * mm, "end": v(23.26, -1.02) * mm});
            skLineSegment(sketch, "E13.19.26.0", {"start": v(24.72, -4.36) * mm, "end": v(22.93, -4.04) * mm});
            skArc(sketch, "E13.22.26.0", {"start": v(24.72, -4.36) * mm, "mid": v(25.04, -4.38) * mm, "end": v(25.36, -4.34) * mm});
            skArc(sketch, "E13.26.26.0", {"start": v(25.36, -4.34) * mm, "mid": v(26.1, -4.12) * mm, "end": v(26.8, -3.81) * mm});
            skArc(sketch, "E13.1.27.0", {"start": v(27.06, 0.9) * mm, "mid": v(27.37, 1.29) * mm, "end": v(27.46, 1.78) * mm});
            skArc(sketch, "E13.4.27.0", {"start": v(27.46, 1.82) * mm, "mid": v(27.3, 2.3) * mm, "end": v(26.94, 2.64) * mm});
            skArc(sketch, "E13.8.27.0", {"start": v(25.52, 3.23) * mm, "mid": v(26.25, 2.98) * mm, "end": v(26.94, 2.64) * mm});
            skArc(sketch, "E13.12.27.0", {"start": v(25.52, 3.23) * mm, "mid": v(25.2, 3.29) * mm, "end": v(24.88, 3.28) * mm});
            skLineSegment(sketch, "E13.16.27.0", {"start": v(24.88, 3.28) * mm, "end": v(23.08, 3.04) * mm});
            skLineSegment(sketch, "E13.19.27.0", {"start": v(25.1, 0) * mm, "end": v(23.28, 0) * mm});
            skArc(sketch, "E13.22.27.0", {"start": v(25.1, 0) * mm, "mid": v(25.42, 0.03) * mm, "end": v(25.73, 0.13) * mm});
            skArc(sketch, "E13.26.27.0", {"start": v(25.73, 0.13) * mm, "mid": v(26.41, 0.47) * mm, "end": v(27.06, 0.9) * mm});
            skArc(sketch, "E13.1.28.0", {"start": v(26.49, 5.59) * mm, "mid": v(26.73, 6.02) * mm, "end": v(26.73, 6.52) * mm});
            skArc(sketch, "E13.4.28.0", {"start": v(26.72, 6.56) * mm, "mid": v(26.49, 7) * mm, "end": v(26.08, 7.28) * mm});
            skArc(sketch, "E13.8.28.0", {"start": v(24.57, 7.61) * mm, "mid": v(25.34, 7.5) * mm, "end": v(26.08, 7.28) * mm});
            skArc(sketch, "E13.12.28.0", {"start": v(24.57, 7.61) * mm, "mid": v(24.25, 7.61) * mm, "end": v(23.94, 7.55) * mm});
            skLineSegment(sketch, "E13.16.28.0", {"start": v(23.94, 7.55) * mm, "end": v(22.2, 7) * mm});
            skLineSegment(sketch, "E13.19.28.0", {"start": v(24.72, 4.36) * mm, "end": v(22.93, 4.04) * mm});
            skArc(sketch, "E13.22.28.0", {"start": v(24.72, 4.36) * mm, "mid": v(25.03, 4.45) * mm, "end": v(25.31, 4.6) * mm});
            skArc(sketch, "E13.26.28.0", {"start": v(25.31, 4.6) * mm, "mid": v(25.93, 5.05) * mm, "end": v(26.49, 5.59) * mm});
            skArc(sketch, "E13.1.29.0", {"start": v(25.12, 10.1) * mm, "mid": v(25.28, 10.57) * mm, "end": v(25.2, 11.06) * mm});
            skArc(sketch, "E13.4.29.0", {"start": v(25.18, 11.1) * mm, "mid": v(24.87, 11.5) * mm, "end": v(24.42, 11.7) * mm});
            skArc(sketch, "E13.8.29.0", {"start": v(22.88, 11.76) * mm, "mid": v(23.65, 11.78) * mm, "end": v(24.42, 11.7) * mm});
            skArc(sketch, "E13.12.29.0", {"start": v(22.88, 11.76) * mm, "mid": v(22.56, 11.7) * mm, "end": v(22.26, 11.59) * mm});
            skLineSegment(sketch, "E13.16.29.0", {"start": v(22.26, 11.59) * mm, "end": v(20.65, 10.75) * mm});
            skLineSegment(sketch, "E13.19.29.0", {"start": v(23.58, 8.58) * mm, "end": v(21.88, 7.96) * mm});
            skArc(sketch, "E13.22.29.0", {"start": v(23.58, 8.58) * mm, "mid": v(23.87, 8.72) * mm, "end": v(24.13, 8.92) * mm});
            skArc(sketch, "E13.26.29.0", {"start": v(24.13, 8.92) * mm, "mid": v(24.66, 9.48) * mm, "end": v(25.12, 10.1) * mm});
            skArc(sketch, "E13.1.30.0", {"start": v(22.98, 14.3) * mm, "mid": v(23.06, 14.8) * mm, "end": v(22.9, 15.27) * mm});
            skArc(sketch, "E13.4.30.0", {"start": v(22.87, 15.3) * mm, "mid": v(22.5, 15.64) * mm, "end": v(22.01, 15.76) * mm});
            skArc(sketch, "E13.8.30.0", {"start": v(20.49, 15.56) * mm, "mid": v(21.25, 15.7) * mm, "end": v(22.01, 15.76) * mm});
            skArc(sketch, "E13.12.30.0", {"start": v(20.49, 15.56) * mm, "mid": v(20.19, 15.45) * mm, "end": v(19.91, 15.28) * mm});
            skLineSegment(sketch, "E13.16.30.0", {"start": v(19.91, 15.28) * mm, "end": v(18.47, 14.17) * mm});
            skLineSegment(sketch, "E13.19.30.0", {"start": v(21.73, 12.55) * mm, "end": v(20.16, 11.64) * mm});
            skArc(sketch, "E13.22.30.0", {"start": v(21.73, 12.55) * mm, "mid": v(22, 12.74) * mm, "end": v(22.21, 12.97) * mm});
            skArc(sketch, "E13.26.30.0", {"start": v(22.21, 12.97) * mm, "mid": v(22.64, 13.62) * mm, "end": v(22.98, 14.3) * mm});
            skArc(sketch, "E13.1.31.0", {"start": v(20.15, 18.08) * mm, "mid": v(20.14, 18.58) * mm, "end": v(19.9, 19.01) * mm});
            skArc(sketch, "E13.4.31.0", {"start": v(19.86, 19.04) * mm, "mid": v(19.44, 19.3) * mm, "end": v(18.94, 19.34) * mm});
            skArc(sketch, "E13.8.31.0", {"start": v(17.48, 18.88) * mm, "mid": v(18.2, 19.15) * mm, "end": v(18.94, 19.34) * mm});
            skArc(sketch, "E13.12.31.0", {"start": v(17.48, 18.88) * mm, "mid": v(17.2, 18.72) * mm, "end": v(16.96, 18.5) * mm});
            skLineSegment(sketch, "E13.16.31.0", {"start": v(16.96, 18.5) * mm, "end": v(15.73, 17.16) * mm});
            skLineSegment(sketch, "E13.19.31.0", {"start": v(19.23, 16.13) * mm, "end": v(17.83, 14.96) * mm});
            skArc(sketch, "E13.22.31.0", {"start": v(19.23, 16.13) * mm, "mid": v(19.45, 16.36) * mm, "end": v(19.62, 16.64) * mm});
            skArc(sketch, "E13.26.31.0", {"start": v(19.62, 16.64) * mm, "mid": v(19.93, 17.34) * mm, "end": v(20.15, 18.08) * mm});
            skArc(sketch, "E13.1.32.0", {"start": v(16.7, 21.3) * mm, "mid": v(16.6, 21.8) * mm, "end": v(16.29, 22.18) * mm});
            skArc(sketch, "E13.4.32.0", {"start": v(16.25, 22.2) * mm, "mid": v(15.8, 22.39) * mm, "end": v(15.3, 22.34) * mm});
            skArc(sketch, "E13.8.32.0", {"start": v(13.93, 21.63) * mm, "mid": v(14.6, 22.02) * mm, "end": v(15.3, 22.34) * mm});
            skArc(sketch, "E13.12.32.0", {"start": v(13.93, 21.63) * mm, "mid": v(13.68, 21.42) * mm, "end": v(13.48, 21.17) * mm});
            skLineSegment(sketch, "E13.16.32.0", {"start": v(13.48, 21.17) * mm, "end": v(12.5, 19.63) * mm});
            skLineSegment(sketch, "E13.19.32.0", {"start": v(16.13, 19.23) * mm, "end": v(14.96, 17.83) * mm});
            skArc(sketch, "E13.22.32.0", {"start": v(16.13, 19.23) * mm, "mid": v(16.31, 19.5) * mm, "end": v(16.44, 19.8) * mm});
            skArc(sketch, "E13.26.32.0", {"start": v(16.44, 19.8) * mm, "mid": v(16.62, 20.54) * mm, "end": v(16.7, 21.3) * mm});
            skArc(sketch, "E13.1.33.0", {"start": v(12.75, 23.88) * mm, "mid": v(12.57, 24.35) * mm, "end": v(12.19, 24.67) * mm});
            skArc(sketch, "E13.4.33.0", {"start": v(12.15, 24.69) * mm, "mid": v(11.66, 24.8) * mm, "end": v(11.19, 24.65) * mm});
            skArc(sketch, "E13.8.33.0", {"start": v(9.96, 23.72) * mm, "mid": v(10.55, 24.22) * mm, "end": v(11.19, 24.65) * mm});
            skArc(sketch, "E13.12.33.0", {"start": v(9.96, 23.72) * mm, "mid": v(9.76, 23.47) * mm, "end": v(9.6, 23.19) * mm});
            skLineSegment(sketch, "E13.16.33.0", {"start": v(9.6, 23.19) * mm, "end": v(8.9, 21.5) * mm});
            skLineSegment(sketch, "E13.19.33.0", {"start": v(12.55, 21.73) * mm, "end": v(11.64, 20.16) * mm});
            skArc(sketch, "E13.22.33.0", {"start": v(12.55, 21.73) * mm, "mid": v(12.68, 22.03) * mm, "end": v(12.75, 22.34) * mm});
            skArc(sketch, "E13.26.33.0", {"start": v(12.75, 22.34) * mm, "mid": v(12.8, 23.11) * mm, "end": v(12.75, 23.88) * mm});
            skArc(sketch, "E13.1.34.0", {"start": v(8.4, 25.73) * mm, "mid": v(8.15, 26.16) * mm, "end": v(7.72, 26.41) * mm});
            skArc(sketch, "E13.4.34.0", {"start": v(7.68, 26.42) * mm, "mid": v(7.18, 26.44) * mm, "end": v(6.74, 26.22) * mm});
            skArc(sketch, "E13.8.34.0", {"start": v(5.7, 25.09) * mm, "mid": v(6.18, 25.69) * mm, "end": v(6.74, 26.22) * mm});
            skArc(sketch, "E13.12.34.0", {"start": v(5.7, 25.09) * mm, "mid": v(5.53, 24.8) * mm, "end": v(5.43, 24.5) * mm});
            skLineSegment(sketch, "E13.16.34.0", {"start": v(5.43, 24.5) * mm, "end": v(5.04, 22.73) * mm});
            skLineSegment(sketch, "E13.19.34.0", {"start": v(8.58, 23.58) * mm, "end": v(7.96, 21.88) * mm});
            skArc(sketch, "E13.22.34.0", {"start": v(8.58, 23.58) * mm, "mid": v(8.66, 23.9) * mm, "end": v(8.68, 24.22) * mm});
            skArc(sketch, "E13.26.34.0", {"start": v(8.68, 24.22) * mm, "mid": v(8.59, 24.98) * mm, "end": v(8.4, 25.73) * mm});
            skArc(sketch, "E13.1.35.0", {"start": v(3.81, 26.8) * mm, "mid": v(3.48, 27.18) * mm, "end": v(3.02, 27.35) * mm});
            skArc(sketch, "E13.4.35.0", {"start": v(2.97, 27.35) * mm, "mid": v(2.48, 27.29) * mm, "end": v(2.08, 27) * mm});
            skArc(sketch, "E13.8.35.0", {"start": v(1.25, 25.7) * mm, "mid": v(1.63, 26.37) * mm, "end": v(2.08, 27) * mm});
            skArc(sketch, "E13.12.35.0", {"start": v(1.25, 25.7) * mm, "mid": v(1.14, 25.4) * mm, "end": v(1.1, 25.07) * mm});
            skLineSegment(sketch, "E13.16.35.0", {"start": v(1.1, 25.07) * mm, "end": v(1.02, 23.26) * mm});
            skLineSegment(sketch, "E13.19.35.0", {"start": v(4.36, 24.72) * mm, "end": v(4.04, 22.93) * mm});
            skArc(sketch, "E13.22.35.0", {"start": v(4.36, 24.72) * mm, "mid": v(4.38, 25.04) * mm, "end": v(4.34, 25.36) * mm});
            skArc(sketch, "E13.26.35.0", {"start": v(4.34, 25.36) * mm, "mid": v(4.12, 26.1) * mm, "end": v(3.81, 26.8) * mm});
            skSolve(sketch);
        }
        {
            var Q0;
            {var subQ0=sQuery(id+"F0.wireOp",EDGE,"E0");var subQ33=makeQuery(id+"F0.imprint","IMPRINT",VERTEX,{"disambiguationData":[OD(52.0)],"derivedFrom":subQ0});Q0=makeQuery(id+"F0.imprint","IMPRINT",FACE,{"disambiguationData":[TD([[makeQuery(id+"F0.imprint","IMPRINT",EDGE,{"disambiguationData":[TD([[subQ33,1.0]])],"derivedFrom":subQ0}),1.0]])]});}
            cPlane(context, id + "F1", {"entities" : qUnion([Q0]), "cplaneType" : CPlaneType.OFFSET, "offset" : 6.35 * mm, "width" : 152.4 * mm, "height" : 152.4 * mm});
        }
        {
            var Q0;
            Q0=qCreatedBy(id+"F1.planeOp",FACE);
            var sketch = newSketch(context, id + "F2", { "sketchPlane" : qUnion([Q0])});
            skArc(sketch, "E14.0.0", {"start": v(23.26, -1.02) * mm, "mid": v(23.27, -0.5) * mm, "end": v(23.28, 0) * mm});
            skArc(sketch, "E14.0.1", {"start": v(23.28, 0) * mm, "mid": v(23.23, 1.52) * mm, "end": v(23.08, 3.04) * mm});
            skArc(sketch, "E14.0.2", {"start": v(23.08, 3.04) * mm, "mid": v(23, 3.54) * mm, "end": v(22.93, 4.04) * mm});
            skArc(sketch, "E14.0.3", {"start": v(22.93, 4.04) * mm, "mid": v(22.61, 5.53) * mm, "end": v(22.2, 7) * mm});
            skArc(sketch, "E14.0.4", {"start": v(22.2, 7) * mm, "mid": v(22.04, 7.48) * mm, "end": v(21.88, 7.96) * mm});
            skArc(sketch, "E14.0.5", {"start": v(21.88, 7.96) * mm, "mid": v(21.3, 9.38) * mm, "end": v(20.65, 10.75) * mm});
            skArc(sketch, "E14.0.6", {"start": v(20.65, 10.75) * mm, "mid": v(20.4, 11.2) * mm, "end": v(20.16, 11.64) * mm});
            skArc(sketch, "E14.0.7", {"start": v(20.16, 11.64) * mm, "mid": v(19.36, 12.93) * mm, "end": v(18.47, 14.17) * mm});
            skArc(sketch, "E14.0.8", {"start": v(18.47, 14.17) * mm, "mid": v(18.16, 14.57) * mm, "end": v(17.83, 14.96) * mm});
            skArc(sketch, "E14.0.9", {"start": v(17.83, 14.96) * mm, "mid": v(16.82, 16.1) * mm, "end": v(15.73, 17.16) * mm});
            skArc(sketch, "E14.0.10", {"start": v(15.73, 17.16) * mm, "mid": v(15.35, 17.5) * mm, "end": v(14.96, 17.83) * mm});
            skArc(sketch, "E14.0.11", {"start": v(14.96, 17.83) * mm, "mid": v(13.77, 18.77) * mm, "end": v(12.5, 19.63) * mm});
            skArc(sketch, "E14.0.12", {"start": v(12.5, 19.63) * mm, "mid": v(12.08, 19.9) * mm, "end": v(11.64, 20.16) * mm});
            skArc(sketch, "E14.0.13", {"start": v(11.64, 20.16) * mm, "mid": v(10.3, 20.88) * mm, "end": v(8.9, 21.5) * mm});
            skArc(sketch, "E14.0.14", {"start": v(8.9, 21.5) * mm, "mid": v(8.44, 21.7) * mm, "end": v(7.96, 21.88) * mm});
            skArc(sketch, "E14.0.15", {"start": v(7.96, 21.88) * mm, "mid": v(6.51, 22.35) * mm, "end": v(5.04, 22.73) * mm});
            skArc(sketch, "E14.0.16", {"start": v(5.04, 22.73) * mm, "mid": v(4.54, 22.83) * mm, "end": v(4.04, 22.93) * mm});
            skArc(sketch, "E14.0.17", {"start": v(4.04, 22.93) * mm, "mid": v(2.53, 23.14) * mm, "end": v(1.02, 23.26) * mm});
            skArc(sketch, "E14.0.18", {"start": v(1.02, 23.26) * mm, "mid": v(0.5, 23.27) * mm, "end": v(0, 23.28) * mm});
            skArc(sketch, "E14.0.19", {"start": v(0, 23.28) * mm, "mid": v(-1.52, 23.23) * mm, "end": v(-3.04, 23.08) * mm});
            skArc(sketch, "E14.0.20", {"start": v(-3.04, 23.08) * mm, "mid": v(-3.54, 23) * mm, "end": v(-4.04, 22.93) * mm});
            skArc(sketch, "E14.0.21", {"start": v(-4.04, 22.93) * mm, "mid": v(-5.53, 22.61) * mm, "end": v(-7, 22.2) * mm});
            skArc(sketch, "E14.0.22", {"start": v(-7, 22.2) * mm, "mid": v(-7.48, 22.04) * mm, "end": v(-7.96, 21.88) * mm});
            skArc(sketch, "E14.0.23", {"start": v(-7.96, 21.88) * mm, "mid": v(-9.38, 21.3) * mm, "end": v(-10.75, 20.65) * mm});
            skArc(sketch, "E14.0.24", {"start": v(-10.75, 20.65) * mm, "mid": v(-11.2, 20.4) * mm, "end": v(-11.64, 20.16) * mm});
            skArc(sketch, "E14.0.25", {"start": v(-11.64, 20.16) * mm, "mid": v(-12.93, 19.36) * mm, "end": v(-14.17, 18.47) * mm});
            skArc(sketch, "E14.0.26", {"start": v(-14.17, 18.47) * mm, "mid": v(-14.57, 18.16) * mm, "end": v(-14.96, 17.83) * mm});
            skArc(sketch, "E14.0.27", {"start": v(-14.96, 17.83) * mm, "mid": v(-16.1, 16.82) * mm, "end": v(-17.16, 15.73) * mm});
            skArc(sketch, "E14.0.28", {"start": v(-17.16, 15.73) * mm, "mid": v(-17.5, 15.35) * mm, "end": v(-17.83, 14.96) * mm});
            skArc(sketch, "E14.0.29", {"start": v(-17.83, 14.96) * mm, "mid": v(-18.77, 13.77) * mm, "end": v(-19.63, 12.5) * mm});
            skArc(sketch, "E14.0.30", {"start": v(-19.63, 12.5) * mm, "mid": v(-19.9, 12.08) * mm, "end": v(-20.16, 11.64) * mm});
            skArc(sketch, "E14.0.31", {"start": v(-20.16, 11.64) * mm, "mid": v(-20.88, 10.3) * mm, "end": v(-21.5, 8.9) * mm});
            skArc(sketch, "E14.0.32", {"start": v(-21.5, 8.9) * mm, "mid": v(-21.7, 8.44) * mm, "end": v(-21.88, 7.96) * mm});
            skArc(sketch, "E14.0.33", {"start": v(-21.88, 7.96) * mm, "mid": v(-22.35, 6.51) * mm, "end": v(-22.73, 5.04) * mm});
            skArc(sketch, "E14.0.34", {"start": v(-22.73, 5.04) * mm, "mid": v(-22.83, 4.54) * mm, "end": v(-22.93, 4.04) * mm});
            skArc(sketch, "E14.0.35", {"start": v(-22.93, 4.04) * mm, "mid": v(-23.14, 2.53) * mm, "end": v(-23.26, 1.02) * mm});
            skArc(sketch, "E14.0.36", {"start": v(-23.26, 1.02) * mm, "mid": v(-23.27, 0.5) * mm, "end": v(-23.28, 0) * mm});
            skArc(sketch, "E14.0.37", {"start": v(-23.28, 0) * mm, "mid": v(-23.23, -1.52) * mm, "end": v(-23.08, -3.04) * mm});
            skArc(sketch, "E14.0.38", {"start": v(-23.08, -3.04) * mm, "mid": v(-23, -3.54) * mm, "end": v(-22.93, -4.04) * mm});
            skArc(sketch, "E14.0.39", {"start": v(-22.93, -4.04) * mm, "mid": v(-22.61, -5.53) * mm, "end": v(-22.2, -7) * mm});
            skArc(sketch, "E14.0.40", {"start": v(-22.2, -7) * mm, "mid": v(-22.04, -7.48) * mm, "end": v(-21.88, -7.96) * mm});
            skArc(sketch, "E14.0.41", {"start": v(-21.88, -7.96) * mm, "mid": v(-21.3, -9.38) * mm, "end": v(-20.65, -10.75) * mm});
            skArc(sketch, "E14.0.42", {"start": v(-20.65, -10.75) * mm, "mid": v(-20.4, -11.2) * mm, "end": v(-20.16, -11.64) * mm});
            skArc(sketch, "E14.0.43", {"start": v(-20.16, -11.64) * mm, "mid": v(-19.36, -12.93) * mm, "end": v(-18.47, -14.17) * mm});
            skArc(sketch, "E14.0.44", {"start": v(-18.47, -14.17) * mm, "mid": v(-18.16, -14.57) * mm, "end": v(-17.83, -14.96) * mm});
            skArc(sketch, "E14.0.45", {"start": v(-17.83, -14.96) * mm, "mid": v(-16.82, -16.1) * mm, "end": v(-15.73, -17.16) * mm});
            skArc(sketch, "E14.0.46", {"start": v(-15.73, -17.16) * mm, "mid": v(-15.35, -17.5) * mm, "end": v(-14.96, -17.83) * mm});
            skArc(sketch, "E14.0.47", {"start": v(-14.96, -17.83) * mm, "mid": v(-13.77, -18.77) * mm, "end": v(-12.5, -19.63) * mm});
            skArc(sketch, "E14.0.48", {"start": v(-12.5, -19.63) * mm, "mid": v(-12.08, -19.9) * mm, "end": v(-11.64, -20.16) * mm});
            skArc(sketch, "E14.0.49", {"start": v(-11.64, -20.16) * mm, "mid": v(-10.3, -20.88) * mm, "end": v(-8.9, -21.5) * mm});
            skArc(sketch, "E14.0.50", {"start": v(-8.9, -21.5) * mm, "mid": v(-8.44, -21.7) * mm, "end": v(-7.96, -21.88) * mm});
            skArc(sketch, "E14.0.51", {"start": v(-7.96, -21.88) * mm, "mid": v(-6.51, -22.35) * mm, "end": v(-5.04, -22.73) * mm});
            skArc(sketch, "E14.0.52", {"start": v(-5.04, -22.73) * mm, "mid": v(-4.54, -22.83) * mm, "end": v(-4.04, -22.93) * mm});
            skArc(sketch, "E14.0.53", {"start": v(-4.04, -22.93) * mm, "mid": v(-2.53, -23.14) * mm, "end": v(-1.02, -23.26) * mm});
            skArc(sketch, "E14.0.54", {"start": v(-1.02, -23.26) * mm, "mid": v(-0.5, -23.27) * mm, "end": v(0, -23.28) * mm});
            skArc(sketch, "E14.0.55", {"start": v(0, -23.28) * mm, "mid": v(1.52, -23.23) * mm, "end": v(3.04, -23.08) * mm});
            skArc(sketch, "E14.0.56", {"start": v(3.04, -23.08) * mm, "mid": v(3.54, -23) * mm, "end": v(4.04, -22.93) * mm});
            skArc(sketch, "E14.0.57", {"start": v(4.04, -22.93) * mm, "mid": v(5.53, -22.61) * mm, "end": v(7, -22.2) * mm});
            skArc(sketch, "E14.0.58", {"start": v(7, -22.2) * mm, "mid": v(7.48, -22.04) * mm, "end": v(7.96, -21.88) * mm});
            skArc(sketch, "E14.0.59", {"start": v(7.96, -21.88) * mm, "mid": v(9.38, -21.3) * mm, "end": v(10.75, -20.65) * mm});
            skArc(sketch, "E14.0.60", {"start": v(10.75, -20.65) * mm, "mid": v(11.2, -20.4) * mm, "end": v(11.64, -20.16) * mm});
            skArc(sketch, "E14.0.61", {"start": v(11.64, -20.16) * mm, "mid": v(12.93, -19.36) * mm, "end": v(14.17, -18.47) * mm});
            skArc(sketch, "E14.0.62", {"start": v(14.17, -18.47) * mm, "mid": v(14.57, -18.16) * mm, "end": v(14.96, -17.83) * mm});
            skArc(sketch, "E14.0.63", {"start": v(14.96, -17.83) * mm, "mid": v(16.1, -16.82) * mm, "end": v(17.16, -15.73) * mm});
            skArc(sketch, "E14.0.64", {"start": v(17.16, -15.73) * mm, "mid": v(17.5, -15.35) * mm, "end": v(17.83, -14.96) * mm});
            skArc(sketch, "E14.0.65", {"start": v(17.83, -14.96) * mm, "mid": v(18.77, -13.77) * mm, "end": v(19.63, -12.5) * mm});
            skArc(sketch, "E14.0.66", {"start": v(19.63, -12.5) * mm, "mid": v(19.9, -12.08) * mm, "end": v(20.16, -11.64) * mm});
            skArc(sketch, "E14.0.67", {"start": v(20.16, -11.64) * mm, "mid": v(20.88, -10.3) * mm, "end": v(21.5, -8.9) * mm});
            skArc(sketch, "E14.0.68", {"start": v(21.5, -8.9) * mm, "mid": v(21.7, -8.44) * mm, "end": v(21.88, -7.96) * mm});
            skArc(sketch, "E14.0.69", {"start": v(21.88, -7.96) * mm, "mid": v(22.35, -6.51) * mm, "end": v(22.73, -5.04) * mm});
            skArc(sketch, "E14.0.70", {"start": v(22.73, -5.04) * mm, "mid": v(22.83, -4.54) * mm, "end": v(22.93, -4.04) * mm});
            skArc(sketch, "E14.0.71", {"start": v(22.93, -4.04) * mm, "mid": v(23.14, -2.53) * mm, "end": v(23.26, -1.02) * mm});
            skArc(sketch, "E15.0.0", {"start": v(-2.64, 26.94) * mm, "mid": v(-2.98, 26.25) * mm, "end": v(-3.23, 25.52) * mm});
            skArc(sketch, "E15.0.1", {"start": v(-3.23, 25.52) * mm, "mid": v(-3.29, 25.2) * mm, "end": v(-3.28, 24.88) * mm});
            skLineSegment(sketch, "E15.0.2", {"start": v(-3.28, 24.88) * mm, "end": v(-3.04, 23.08) * mm});
            skArc(sketch, "E15.0.3", {"start": v(-3.04, 23.08) * mm, "mid": v(-1.52, 23.23) * mm, "end": v(0, 23.28) * mm});
            skLineSegment(sketch, "E15.0.4", {"start": v(0, 23.28) * mm, "end": v(0, 25.1) * mm});
            skArc(sketch, "E15.0.5", {"start": v(0, 25.1) * mm, "mid": v(-0.03, 25.42) * mm, "end": v(-0.13, 25.73) * mm});
            skArc(sketch, "E15.0.6", {"start": v(-0.13, 25.73) * mm, "mid": v(-0.47, 26.41) * mm, "end": v(-0.9, 27.06) * mm});
            skArc(sketch, "E15.0.7", {"start": v(-0.9, 27.06) * mm, "mid": v(-1.29, 27.37) * mm, "end": v(-1.78, 27.46) * mm});
            skLineSegment(sketch, "E15.0.8", {"start": v(-1.78, 27.46) * mm, "end": v(-1.8, 27.46) * mm});
            skLineSegment(sketch, "E15.0.9", {"start": v(-1.8, 27.46) * mm, "end": v(-1.82, 27.46) * mm});
            skArc(sketch, "E15.0.10", {"start": v(-1.82, 27.46) * mm, "mid": v(-2.3, 27.3) * mm, "end": v(-2.64, 26.94) * mm});
            skSolve(sketch);
        }
        {
            var Q0;
            Q0=makeQuery(id+"F2.imprint","IMPRINT",FACE,{"disambiguationData":[TD([[makeQuery(id+"F2.imprint","IMPRINT",EDGE,{"derivedFrom":sQuery(id+"F2.wireOp",EDGE,"E15.0.0")}),1.0]])]});
            var Q1;
            Q1=makeQuery(id+"F0.imprint","IMPRINT",FACE,{"disambiguationData":[TD([[makeQuery(id+"F0.imprint","IMPRINT",EDGE,{"derivedFrom":sQuery(id+"F0.wireOp",EDGE,"E1.trimOffspring")}),1.0]])]});
            loft(context, id + "F3", {"sheetProfilesArray" : [{ "sheetProfileEntities" : qUnion([Q0]) }, { "sheetProfileEntities" : qUnion([Q1]) }]});
        }
        {
            var Q0;
            Q0=qCreatedBy(id+"F1.planeOp",FACE);
            var sketch = newSketch(context, id + "F4", { "sketchPlane" : qUnion([Q0])});
            skCircle(sketch, "E16", {"center": v(0, 0) * mm, "radius": 23.28 * mm});
            skSolve(sketch);
        }
        {
            var Q0;
            Q0 = qSketchRegion(id + "F4", true);
            var Q1;
            Q1=makeQuery(id+"F3.opLoft","CAP_FACE",FACE,{"disambiguationData":[OSD([makeQuery(id+"F0.imprint","IMPRINT",FACE,{"disambiguationData":[TD([[makeQuery(id+"F0.imprint","IMPRINT",EDGE,{"derivedFrom":sQuery(id+"F0.wireOp",EDGE,"E1.trimOffspring")}),1.0]])]})])],"isStart":true});
            extrude(context, id + "F5", {"entities" : qUnion([Q0]), "operationType" : NewBodyOperationType.ADD, "endBound" : BoundingType.UP_TO_SURFACE, "oppositeDirection" : true, "endBoundEntityFace" : qUnion([Q1]), "depth" : 25.4 * mm});
        }
        {
            var Q0;
            Q0=makeQuery(id+"F3.opLoft","SWEPT_BODY",BODY,{"disambiguationData":[OSD([makeQuery(id+"F0.imprint","IMPRINT",FACE,{"disambiguationData":[TD([[makeQuery(id+"F0.imprint","IMPRINT",EDGE,{"derivedFrom":sQuery(id+"F0.wireOp",EDGE,"E1.trimOffspring")}),1.0]])]}),makeQuery(id+"F2.imprint","IMPRINT",FACE,{"disambiguationData":[TD([[makeQuery(id+"F2.imprint","IMPRINT",EDGE,{"derivedFrom":sQuery(id+"F2.wireOp",EDGE,"E15.0.0")}),1.0]])]})])]});
            var Q1;
            Q1=makeQuery(id+"F5.opExtrude","SWEPT_FACE",FACE,{"disambiguationData":[OSD([sQuery(id+"F4.wireOp",EDGE,"E16")])]});
            circularPattern(context, id + "F6", {"entities" : qUnion([Q0]), "axis" : qUnion([Q1]), "angle" : 360 * degree, "instanceCount" : 36, "equalSpace" : true});
        }
        {
            var Q0;
            Q0=makeQuery(id+"F6.opPattern","COPY",BODY,{"derivedFrom":makeQuery(id+"F3.opLoft","SWEPT_BODY",BODY,{"disambiguationData":[OSD([makeQuery(id+"F0.imprint","IMPRINT",FACE,{"disambiguationData":[TD([[makeQuery(id+"F0.imprint","IMPRINT",EDGE,{"derivedFrom":sQuery(id+"F0.wireOp",EDGE,"E1.trimOffspring")}),1.0]])]}),makeQuery(id+"F2.imprint","IMPRINT",FACE,{"disambiguationData":[TD([[makeQuery(id+"F2.imprint","IMPRINT",EDGE,{"derivedFrom":sQuery(id+"F2.wireOp",EDGE,"E15.0.0")}),1.0]])]})])]}),"instanceName":"31"});
            var Q1;
            Q1=makeQuery(id+"F6.opPattern","COPY",BODY,{"derivedFrom":makeQuery(id+"F3.opLoft","SWEPT_BODY",BODY,{"disambiguationData":[OSD([makeQuery(id+"F0.imprint","IMPRINT",FACE,{"disambiguationData":[TD([[makeQuery(id+"F0.imprint","IMPRINT",EDGE,{"derivedFrom":sQuery(id+"F0.wireOp",EDGE,"E1.trimOffspring")}),1.0]])]}),makeQuery(id+"F2.imprint","IMPRINT",FACE,{"disambiguationData":[TD([[makeQuery(id+"F2.imprint","IMPRINT",EDGE,{"derivedFrom":sQuery(id+"F2.wireOp",EDGE,"E15.0.0")}),1.0]])]})])]}),"instanceName":"2"});
            var Q2;
            Q2=makeQuery(id+"F3.opLoft","SWEPT_BODY",BODY,{"disambiguationData":[OSD([makeQuery(id+"F0.imprint","IMPRINT",FACE,{"disambiguationData":[TD([[makeQuery(id+"F0.imprint","IMPRINT",EDGE,{"derivedFrom":sQuery(id+"F0.wireOp",EDGE,"E1.trimOffspring")}),1.0]])]}),makeQuery(id+"F2.imprint","IMPRINT",FACE,{"disambiguationData":[TD([[makeQuery(id+"F2.imprint","IMPRINT",EDGE,{"derivedFrom":sQuery(id+"F2.wireOp",EDGE,"E15.0.0")}),1.0]])]})])]});
            var Q3;
            Q3=makeQuery(id+"F6.opPattern","COPY",BODY,{"derivedFrom":makeQuery(id+"F3.opLoft","SWEPT_BODY",BODY,{"disambiguationData":[OSD([makeQuery(id+"F0.imprint","IMPRINT",FACE,{"disambiguationData":[TD([[makeQuery(id+"F0.imprint","IMPRINT",EDGE,{"derivedFrom":sQuery(id+"F0.wireOp",EDGE,"E1.trimOffspring")}),1.0]])]}),makeQuery(id+"F2.imprint","IMPRINT",FACE,{"disambiguationData":[TD([[makeQuery(id+"F2.imprint","IMPRINT",EDGE,{"derivedFrom":sQuery(id+"F2.wireOp",EDGE,"E15.0.0")}),1.0]])]})])]}),"instanceName":"1"});
            var Q4;
            Q4=makeQuery(id+"F6.opPattern","COPY",BODY,{"derivedFrom":makeQuery(id+"F3.opLoft","SWEPT_BODY",BODY,{"disambiguationData":[OSD([makeQuery(id+"F0.imprint","IMPRINT",FACE,{"disambiguationData":[TD([[makeQuery(id+"F0.imprint","IMPRINT",EDGE,{"derivedFrom":sQuery(id+"F0.wireOp",EDGE,"E1.trimOffspring")}),1.0]])]}),makeQuery(id+"F2.imprint","IMPRINT",FACE,{"disambiguationData":[TD([[makeQuery(id+"F2.imprint","IMPRINT",EDGE,{"derivedFrom":sQuery(id+"F2.wireOp",EDGE,"E15.0.0")}),1.0]])]})])]}),"instanceName":"35"});
            var Q5;
            Q5=makeQuery(id+"F6.opPattern","COPY",BODY,{"derivedFrom":makeQuery(id+"F3.opLoft","SWEPT_BODY",BODY,{"disambiguationData":[OSD([makeQuery(id+"F0.imprint","IMPRINT",FACE,{"disambiguationData":[TD([[makeQuery(id+"F0.imprint","IMPRINT",EDGE,{"derivedFrom":sQuery(id+"F0.wireOp",EDGE,"E1.trimOffspring")}),1.0]])]}),makeQuery(id+"F2.imprint","IMPRINT",FACE,{"disambiguationData":[TD([[makeQuery(id+"F2.imprint","IMPRINT",EDGE,{"derivedFrom":sQuery(id+"F2.wireOp",EDGE,"E15.0.0")}),1.0]])]})])]}),"instanceName":"34"});
            var Q6;
            Q6=makeQuery(id+"F6.opPattern","COPY",BODY,{"derivedFrom":makeQuery(id+"F3.opLoft","SWEPT_BODY",BODY,{"disambiguationData":[OSD([makeQuery(id+"F0.imprint","IMPRINT",FACE,{"disambiguationData":[TD([[makeQuery(id+"F0.imprint","IMPRINT",EDGE,{"derivedFrom":sQuery(id+"F0.wireOp",EDGE,"E1.trimOffspring")}),1.0]])]}),makeQuery(id+"F2.imprint","IMPRINT",FACE,{"disambiguationData":[TD([[makeQuery(id+"F2.imprint","IMPRINT",EDGE,{"derivedFrom":sQuery(id+"F2.wireOp",EDGE,"E15.0.0")}),1.0]])]})])]}),"instanceName":"33"});
            var Q7;
            Q7=makeQuery(id+"F6.opPattern","COPY",BODY,{"derivedFrom":makeQuery(id+"F3.opLoft","SWEPT_BODY",BODY,{"disambiguationData":[OSD([makeQuery(id+"F0.imprint","IMPRINT",FACE,{"disambiguationData":[TD([[makeQuery(id+"F0.imprint","IMPRINT",EDGE,{"derivedFrom":sQuery(id+"F0.wireOp",EDGE,"E1.trimOffspring")}),1.0]])]}),makeQuery(id+"F2.imprint","IMPRINT",FACE,{"disambiguationData":[TD([[makeQuery(id+"F2.imprint","IMPRINT",EDGE,{"derivedFrom":sQuery(id+"F2.wireOp",EDGE,"E15.0.0")}),1.0]])]})])]}),"instanceName":"32"});
            var Q8;
            Q8=makeQuery(id+"F6.opPattern","COPY",BODY,{"derivedFrom":makeQuery(id+"F3.opLoft","SWEPT_BODY",BODY,{"disambiguationData":[OSD([makeQuery(id+"F0.imprint","IMPRINT",FACE,{"disambiguationData":[TD([[makeQuery(id+"F0.imprint","IMPRINT",EDGE,{"derivedFrom":sQuery(id+"F0.wireOp",EDGE,"E1.trimOffspring")}),1.0]])]}),makeQuery(id+"F2.imprint","IMPRINT",FACE,{"disambiguationData":[TD([[makeQuery(id+"F2.imprint","IMPRINT",EDGE,{"derivedFrom":sQuery(id+"F2.wireOp",EDGE,"E15.0.0")}),1.0]])]})])]}),"instanceName":"30"});
            var Q9;
            Q9=makeQuery(id+"F6.opPattern","COPY",BODY,{"derivedFrom":makeQuery(id+"F3.opLoft","SWEPT_BODY",BODY,{"disambiguationData":[OSD([makeQuery(id+"F0.imprint","IMPRINT",FACE,{"disambiguationData":[TD([[makeQuery(id+"F0.imprint","IMPRINT",EDGE,{"derivedFrom":sQuery(id+"F0.wireOp",EDGE,"E1.trimOffspring")}),1.0]])]}),makeQuery(id+"F2.imprint","IMPRINT",FACE,{"disambiguationData":[TD([[makeQuery(id+"F2.imprint","IMPRINT",EDGE,{"derivedFrom":sQuery(id+"F2.wireOp",EDGE,"E15.0.0")}),1.0]])]})])]}),"instanceName":"29"});
            var Q10;
            Q10=makeQuery(id+"F6.opPattern","COPY",BODY,{"derivedFrom":makeQuery(id+"F3.opLoft","SWEPT_BODY",BODY,{"disambiguationData":[OSD([makeQuery(id+"F0.imprint","IMPRINT",FACE,{"disambiguationData":[TD([[makeQuery(id+"F0.imprint","IMPRINT",EDGE,{"derivedFrom":sQuery(id+"F0.wireOp",EDGE,"E1.trimOffspring")}),1.0]])]}),makeQuery(id+"F2.imprint","IMPRINT",FACE,{"disambiguationData":[TD([[makeQuery(id+"F2.imprint","IMPRINT",EDGE,{"derivedFrom":sQuery(id+"F2.wireOp",EDGE,"E15.0.0")}),1.0]])]})])]}),"instanceName":"28"});
            var Q11;
            Q11=makeQuery(id+"F6.opPattern","COPY",BODY,{"derivedFrom":makeQuery(id+"F3.opLoft","SWEPT_BODY",BODY,{"disambiguationData":[OSD([makeQuery(id+"F0.imprint","IMPRINT",FACE,{"disambiguationData":[TD([[makeQuery(id+"F0.imprint","IMPRINT",EDGE,{"derivedFrom":sQuery(id+"F0.wireOp",EDGE,"E1.trimOffspring")}),1.0]])]}),makeQuery(id+"F2.imprint","IMPRINT",FACE,{"disambiguationData":[TD([[makeQuery(id+"F2.imprint","IMPRINT",EDGE,{"derivedFrom":sQuery(id+"F2.wireOp",EDGE,"E15.0.0")}),1.0]])]})])]}),"instanceName":"27"});
            var Q12;
            Q12=makeQuery(id+"F6.opPattern","COPY",BODY,{"derivedFrom":makeQuery(id+"F3.opLoft","SWEPT_BODY",BODY,{"disambiguationData":[OSD([makeQuery(id+"F0.imprint","IMPRINT",FACE,{"disambiguationData":[TD([[makeQuery(id+"F0.imprint","IMPRINT",EDGE,{"derivedFrom":sQuery(id+"F0.wireOp",EDGE,"E1.trimOffspring")}),1.0]])]}),makeQuery(id+"F2.imprint","IMPRINT",FACE,{"disambiguationData":[TD([[makeQuery(id+"F2.imprint","IMPRINT",EDGE,{"derivedFrom":sQuery(id+"F2.wireOp",EDGE,"E15.0.0")}),1.0]])]})])]}),"instanceName":"26"});
            var Q13;
            Q13=makeQuery(id+"F6.opPattern","COPY",BODY,{"derivedFrom":makeQuery(id+"F3.opLoft","SWEPT_BODY",BODY,{"disambiguationData":[OSD([makeQuery(id+"F0.imprint","IMPRINT",FACE,{"disambiguationData":[TD([[makeQuery(id+"F0.imprint","IMPRINT",EDGE,{"derivedFrom":sQuery(id+"F0.wireOp",EDGE,"E1.trimOffspring")}),1.0]])]}),makeQuery(id+"F2.imprint","IMPRINT",FACE,{"disambiguationData":[TD([[makeQuery(id+"F2.imprint","IMPRINT",EDGE,{"derivedFrom":sQuery(id+"F2.wireOp",EDGE,"E15.0.0")}),1.0]])]})])]}),"instanceName":"25"});
            var Q14;
            Q14=makeQuery(id+"F6.opPattern","COPY",BODY,{"derivedFrom":makeQuery(id+"F3.opLoft","SWEPT_BODY",BODY,{"disambiguationData":[OSD([makeQuery(id+"F0.imprint","IMPRINT",FACE,{"disambiguationData":[TD([[makeQuery(id+"F0.imprint","IMPRINT",EDGE,{"derivedFrom":sQuery(id+"F0.wireOp",EDGE,"E1.trimOffspring")}),1.0]])]}),makeQuery(id+"F2.imprint","IMPRINT",FACE,{"disambiguationData":[TD([[makeQuery(id+"F2.imprint","IMPRINT",EDGE,{"derivedFrom":sQuery(id+"F2.wireOp",EDGE,"E15.0.0")}),1.0]])]})])]}),"instanceName":"24"});
            var Q15;
            Q15=makeQuery(id+"F6.opPattern","COPY",BODY,{"derivedFrom":makeQuery(id+"F3.opLoft","SWEPT_BODY",BODY,{"disambiguationData":[OSD([makeQuery(id+"F0.imprint","IMPRINT",FACE,{"disambiguationData":[TD([[makeQuery(id+"F0.imprint","IMPRINT",EDGE,{"derivedFrom":sQuery(id+"F0.wireOp",EDGE,"E1.trimOffspring")}),1.0]])]}),makeQuery(id+"F2.imprint","IMPRINT",FACE,{"disambiguationData":[TD([[makeQuery(id+"F2.imprint","IMPRINT",EDGE,{"derivedFrom":sQuery(id+"F2.wireOp",EDGE,"E15.0.0")}),1.0]])]})])]}),"instanceName":"23"});
            var Q16;
            Q16=makeQuery(id+"F6.opPattern","COPY",BODY,{"derivedFrom":makeQuery(id+"F3.opLoft","SWEPT_BODY",BODY,{"disambiguationData":[OSD([makeQuery(id+"F0.imprint","IMPRINT",FACE,{"disambiguationData":[TD([[makeQuery(id+"F0.imprint","IMPRINT",EDGE,{"derivedFrom":sQuery(id+"F0.wireOp",EDGE,"E1.trimOffspring")}),1.0]])]}),makeQuery(id+"F2.imprint","IMPRINT",FACE,{"disambiguationData":[TD([[makeQuery(id+"F2.imprint","IMPRINT",EDGE,{"derivedFrom":sQuery(id+"F2.wireOp",EDGE,"E15.0.0")}),1.0]])]})])]}),"instanceName":"22"});
            var Q17;
            Q17=makeQuery(id+"F6.opPattern","COPY",BODY,{"derivedFrom":makeQuery(id+"F3.opLoft","SWEPT_BODY",BODY,{"disambiguationData":[OSD([makeQuery(id+"F0.imprint","IMPRINT",FACE,{"disambiguationData":[TD([[makeQuery(id+"F0.imprint","IMPRINT",EDGE,{"derivedFrom":sQuery(id+"F0.wireOp",EDGE,"E1.trimOffspring")}),1.0]])]}),makeQuery(id+"F2.imprint","IMPRINT",FACE,{"disambiguationData":[TD([[makeQuery(id+"F2.imprint","IMPRINT",EDGE,{"derivedFrom":sQuery(id+"F2.wireOp",EDGE,"E15.0.0")}),1.0]])]})])]}),"instanceName":"21"});
            var Q18;
            Q18=makeQuery(id+"F6.opPattern","COPY",BODY,{"derivedFrom":makeQuery(id+"F3.opLoft","SWEPT_BODY",BODY,{"disambiguationData":[OSD([makeQuery(id+"F0.imprint","IMPRINT",FACE,{"disambiguationData":[TD([[makeQuery(id+"F0.imprint","IMPRINT",EDGE,{"derivedFrom":sQuery(id+"F0.wireOp",EDGE,"E1.trimOffspring")}),1.0]])]}),makeQuery(id+"F2.imprint","IMPRINT",FACE,{"disambiguationData":[TD([[makeQuery(id+"F2.imprint","IMPRINT",EDGE,{"derivedFrom":sQuery(id+"F2.wireOp",EDGE,"E15.0.0")}),1.0]])]})])]}),"instanceName":"20"});
            var Q19;
            Q19=makeQuery(id+"F6.opPattern","COPY",BODY,{"derivedFrom":makeQuery(id+"F3.opLoft","SWEPT_BODY",BODY,{"disambiguationData":[OSD([makeQuery(id+"F0.imprint","IMPRINT",FACE,{"disambiguationData":[TD([[makeQuery(id+"F0.imprint","IMPRINT",EDGE,{"derivedFrom":sQuery(id+"F0.wireOp",EDGE,"E1.trimOffspring")}),1.0]])]}),makeQuery(id+"F2.imprint","IMPRINT",FACE,{"disambiguationData":[TD([[makeQuery(id+"F2.imprint","IMPRINT",EDGE,{"derivedFrom":sQuery(id+"F2.wireOp",EDGE,"E15.0.0")}),1.0]])]})])]}),"instanceName":"19"});
            var Q20;
            Q20=makeQuery(id+"F6.opPattern","COPY",BODY,{"derivedFrom":makeQuery(id+"F3.opLoft","SWEPT_BODY",BODY,{"disambiguationData":[OSD([makeQuery(id+"F0.imprint","IMPRINT",FACE,{"disambiguationData":[TD([[makeQuery(id+"F0.imprint","IMPRINT",EDGE,{"derivedFrom":sQuery(id+"F0.wireOp",EDGE,"E1.trimOffspring")}),1.0]])]}),makeQuery(id+"F2.imprint","IMPRINT",FACE,{"disambiguationData":[TD([[makeQuery(id+"F2.imprint","IMPRINT",EDGE,{"derivedFrom":sQuery(id+"F2.wireOp",EDGE,"E15.0.0")}),1.0]])]})])]}),"instanceName":"18"});
            var Q21;
            Q21=makeQuery(id+"F6.opPattern","COPY",BODY,{"derivedFrom":makeQuery(id+"F3.opLoft","SWEPT_BODY",BODY,{"disambiguationData":[OSD([makeQuery(id+"F0.imprint","IMPRINT",FACE,{"disambiguationData":[TD([[makeQuery(id+"F0.imprint","IMPRINT",EDGE,{"derivedFrom":sQuery(id+"F0.wireOp",EDGE,"E1.trimOffspring")}),1.0]])]}),makeQuery(id+"F2.imprint","IMPRINT",FACE,{"disambiguationData":[TD([[makeQuery(id+"F2.imprint","IMPRINT",EDGE,{"derivedFrom":sQuery(id+"F2.wireOp",EDGE,"E15.0.0")}),1.0]])]})])]}),"instanceName":"17"});
            var Q22;
            Q22=makeQuery(id+"F6.opPattern","COPY",BODY,{"derivedFrom":makeQuery(id+"F3.opLoft","SWEPT_BODY",BODY,{"disambiguationData":[OSD([makeQuery(id+"F0.imprint","IMPRINT",FACE,{"disambiguationData":[TD([[makeQuery(id+"F0.imprint","IMPRINT",EDGE,{"derivedFrom":sQuery(id+"F0.wireOp",EDGE,"E1.trimOffspring")}),1.0]])]}),makeQuery(id+"F2.imprint","IMPRINT",FACE,{"disambiguationData":[TD([[makeQuery(id+"F2.imprint","IMPRINT",EDGE,{"derivedFrom":sQuery(id+"F2.wireOp",EDGE,"E15.0.0")}),1.0]])]})])]}),"instanceName":"16"});
            var Q23;
            Q23=makeQuery(id+"F6.opPattern","COPY",BODY,{"derivedFrom":makeQuery(id+"F3.opLoft","SWEPT_BODY",BODY,{"disambiguationData":[OSD([makeQuery(id+"F0.imprint","IMPRINT",FACE,{"disambiguationData":[TD([[makeQuery(id+"F0.imprint","IMPRINT",EDGE,{"derivedFrom":sQuery(id+"F0.wireOp",EDGE,"E1.trimOffspring")}),1.0]])]}),makeQuery(id+"F2.imprint","IMPRINT",FACE,{"disambiguationData":[TD([[makeQuery(id+"F2.imprint","IMPRINT",EDGE,{"derivedFrom":sQuery(id+"F2.wireOp",EDGE,"E15.0.0")}),1.0]])]})])]}),"instanceName":"15"});
            var Q24;
            Q24=makeQuery(id+"F6.opPattern","COPY",BODY,{"derivedFrom":makeQuery(id+"F3.opLoft","SWEPT_BODY",BODY,{"disambiguationData":[OSD([makeQuery(id+"F0.imprint","IMPRINT",FACE,{"disambiguationData":[TD([[makeQuery(id+"F0.imprint","IMPRINT",EDGE,{"derivedFrom":sQuery(id+"F0.wireOp",EDGE,"E1.trimOffspring")}),1.0]])]}),makeQuery(id+"F2.imprint","IMPRINT",FACE,{"disambiguationData":[TD([[makeQuery(id+"F2.imprint","IMPRINT",EDGE,{"derivedFrom":sQuery(id+"F2.wireOp",EDGE,"E15.0.0")}),1.0]])]})])]}),"instanceName":"14"});
            var Q25;
            Q25=makeQuery(id+"F6.opPattern","COPY",BODY,{"derivedFrom":makeQuery(id+"F3.opLoft","SWEPT_BODY",BODY,{"disambiguationData":[OSD([makeQuery(id+"F0.imprint","IMPRINT",FACE,{"disambiguationData":[TD([[makeQuery(id+"F0.imprint","IMPRINT",EDGE,{"derivedFrom":sQuery(id+"F0.wireOp",EDGE,"E1.trimOffspring")}),1.0]])]}),makeQuery(id+"F2.imprint","IMPRINT",FACE,{"disambiguationData":[TD([[makeQuery(id+"F2.imprint","IMPRINT",EDGE,{"derivedFrom":sQuery(id+"F2.wireOp",EDGE,"E15.0.0")}),1.0]])]})])]}),"instanceName":"13"});
            var Q26;
            Q26=makeQuery(id+"F6.opPattern","COPY",BODY,{"derivedFrom":makeQuery(id+"F3.opLoft","SWEPT_BODY",BODY,{"disambiguationData":[OSD([makeQuery(id+"F0.imprint","IMPRINT",FACE,{"disambiguationData":[TD([[makeQuery(id+"F0.imprint","IMPRINT",EDGE,{"derivedFrom":sQuery(id+"F0.wireOp",EDGE,"E1.trimOffspring")}),1.0]])]}),makeQuery(id+"F2.imprint","IMPRINT",FACE,{"disambiguationData":[TD([[makeQuery(id+"F2.imprint","IMPRINT",EDGE,{"derivedFrom":sQuery(id+"F2.wireOp",EDGE,"E15.0.0")}),1.0]])]})])]}),"instanceName":"12"});
            var Q27;
            Q27=makeQuery(id+"F6.opPattern","COPY",BODY,{"derivedFrom":makeQuery(id+"F3.opLoft","SWEPT_BODY",BODY,{"disambiguationData":[OSD([makeQuery(id+"F0.imprint","IMPRINT",FACE,{"disambiguationData":[TD([[makeQuery(id+"F0.imprint","IMPRINT",EDGE,{"derivedFrom":sQuery(id+"F0.wireOp",EDGE,"E1.trimOffspring")}),1.0]])]}),makeQuery(id+"F2.imprint","IMPRINT",FACE,{"disambiguationData":[TD([[makeQuery(id+"F2.imprint","IMPRINT",EDGE,{"derivedFrom":sQuery(id+"F2.wireOp",EDGE,"E15.0.0")}),1.0]])]})])]}),"instanceName":"11"});
            var Q28;
            Q28=makeQuery(id+"F6.opPattern","COPY",BODY,{"derivedFrom":makeQuery(id+"F3.opLoft","SWEPT_BODY",BODY,{"disambiguationData":[OSD([makeQuery(id+"F0.imprint","IMPRINT",FACE,{"disambiguationData":[TD([[makeQuery(id+"F0.imprint","IMPRINT",EDGE,{"derivedFrom":sQuery(id+"F0.wireOp",EDGE,"E1.trimOffspring")}),1.0]])]}),makeQuery(id+"F2.imprint","IMPRINT",FACE,{"disambiguationData":[TD([[makeQuery(id+"F2.imprint","IMPRINT",EDGE,{"derivedFrom":sQuery(id+"F2.wireOp",EDGE,"E15.0.0")}),1.0]])]})])]}),"instanceName":"10"});
            var Q29;
            Q29=makeQuery(id+"F6.opPattern","COPY",BODY,{"derivedFrom":makeQuery(id+"F3.opLoft","SWEPT_BODY",BODY,{"disambiguationData":[OSD([makeQuery(id+"F0.imprint","IMPRINT",FACE,{"disambiguationData":[TD([[makeQuery(id+"F0.imprint","IMPRINT",EDGE,{"derivedFrom":sQuery(id+"F0.wireOp",EDGE,"E1.trimOffspring")}),1.0]])]}),makeQuery(id+"F2.imprint","IMPRINT",FACE,{"disambiguationData":[TD([[makeQuery(id+"F2.imprint","IMPRINT",EDGE,{"derivedFrom":sQuery(id+"F2.wireOp",EDGE,"E15.0.0")}),1.0]])]})])]}),"instanceName":"9"});
            var Q30;
            Q30=makeQuery(id+"F6.opPattern","COPY",BODY,{"derivedFrom":makeQuery(id+"F3.opLoft","SWEPT_BODY",BODY,{"disambiguationData":[OSD([makeQuery(id+"F0.imprint","IMPRINT",FACE,{"disambiguationData":[TD([[makeQuery(id+"F0.imprint","IMPRINT",EDGE,{"derivedFrom":sQuery(id+"F0.wireOp",EDGE,"E1.trimOffspring")}),1.0]])]}),makeQuery(id+"F2.imprint","IMPRINT",FACE,{"disambiguationData":[TD([[makeQuery(id+"F2.imprint","IMPRINT",EDGE,{"derivedFrom":sQuery(id+"F2.wireOp",EDGE,"E15.0.0")}),1.0]])]})])]}),"instanceName":"8"});
            var Q31;
            Q31=makeQuery(id+"F6.opPattern","COPY",BODY,{"derivedFrom":makeQuery(id+"F3.opLoft","SWEPT_BODY",BODY,{"disambiguationData":[OSD([makeQuery(id+"F0.imprint","IMPRINT",FACE,{"disambiguationData":[TD([[makeQuery(id+"F0.imprint","IMPRINT",EDGE,{"derivedFrom":sQuery(id+"F0.wireOp",EDGE,"E1.trimOffspring")}),1.0]])]}),makeQuery(id+"F2.imprint","IMPRINT",FACE,{"disambiguationData":[TD([[makeQuery(id+"F2.imprint","IMPRINT",EDGE,{"derivedFrom":sQuery(id+"F2.wireOp",EDGE,"E15.0.0")}),1.0]])]})])]}),"instanceName":"7"});
            var Q32;
            Q32=makeQuery(id+"F6.opPattern","COPY",BODY,{"derivedFrom":makeQuery(id+"F3.opLoft","SWEPT_BODY",BODY,{"disambiguationData":[OSD([makeQuery(id+"F0.imprint","IMPRINT",FACE,{"disambiguationData":[TD([[makeQuery(id+"F0.imprint","IMPRINT",EDGE,{"derivedFrom":sQuery(id+"F0.wireOp",EDGE,"E1.trimOffspring")}),1.0]])]}),makeQuery(id+"F2.imprint","IMPRINT",FACE,{"disambiguationData":[TD([[makeQuery(id+"F2.imprint","IMPRINT",EDGE,{"derivedFrom":sQuery(id+"F2.wireOp",EDGE,"E15.0.0")}),1.0]])]})])]}),"instanceName":"6"});
            var Q33;
            Q33=makeQuery(id+"F6.opPattern","COPY",BODY,{"derivedFrom":makeQuery(id+"F3.opLoft","SWEPT_BODY",BODY,{"disambiguationData":[OSD([makeQuery(id+"F0.imprint","IMPRINT",FACE,{"disambiguationData":[TD([[makeQuery(id+"F0.imprint","IMPRINT",EDGE,{"derivedFrom":sQuery(id+"F0.wireOp",EDGE,"E1.trimOffspring")}),1.0]])]}),makeQuery(id+"F2.imprint","IMPRINT",FACE,{"disambiguationData":[TD([[makeQuery(id+"F2.imprint","IMPRINT",EDGE,{"derivedFrom":sQuery(id+"F2.wireOp",EDGE,"E15.0.0")}),1.0]])]})])]}),"instanceName":"5"});
            var Q34;
            Q34=makeQuery(id+"F6.opPattern","COPY",BODY,{"derivedFrom":makeQuery(id+"F3.opLoft","SWEPT_BODY",BODY,{"disambiguationData":[OSD([makeQuery(id+"F0.imprint","IMPRINT",FACE,{"disambiguationData":[TD([[makeQuery(id+"F0.imprint","IMPRINT",EDGE,{"derivedFrom":sQuery(id+"F0.wireOp",EDGE,"E1.trimOffspring")}),1.0]])]}),makeQuery(id+"F2.imprint","IMPRINT",FACE,{"disambiguationData":[TD([[makeQuery(id+"F2.imprint","IMPRINT",EDGE,{"derivedFrom":sQuery(id+"F2.wireOp",EDGE,"E15.0.0")}),1.0]])]})])]}),"instanceName":"4"});
            var Q35;
            Q35=makeQuery(id+"F6.opPattern","COPY",BODY,{"derivedFrom":makeQuery(id+"F3.opLoft","SWEPT_BODY",BODY,{"disambiguationData":[OSD([makeQuery(id+"F0.imprint","IMPRINT",FACE,{"disambiguationData":[TD([[makeQuery(id+"F0.imprint","IMPRINT",EDGE,{"derivedFrom":sQuery(id+"F0.wireOp",EDGE,"E1.trimOffspring")}),1.0]])]}),makeQuery(id+"F2.imprint","IMPRINT",FACE,{"disambiguationData":[TD([[makeQuery(id+"F2.imprint","IMPRINT",EDGE,{"derivedFrom":sQuery(id+"F2.wireOp",EDGE,"E15.0.0")}),1.0]])]})])]}),"instanceName":"3"});
            booleanBodies(context, id + "F7", {"operationType" : BooleanOperationType.UNION, "tools" : qUnion([Q0, Q1, Q2, Q3, Q4, Q5, Q6, Q7, Q8, Q9, Q10, Q11, Q12, Q13, Q14, Q15, Q16, Q17, Q18, Q19, Q20, Q21, Q22, Q23, Q24, Q25, Q26, Q27, Q28, Q29, Q30, Q31, Q32, Q33, Q34, Q35])});
        }
        {
            var Q0;
            {var subQ0=makeQuery(id+"F5.boolean.opBoolean","MERGE",FACE,{"derivedFrom":[makeQuery(id+"F3.opLoft","CAP_FACE",FACE,{"disambiguationData":[OSD([makeQuery(id+"F2.imprint","IMPRINT",FACE,{"disambiguationData":[TD([[makeQuery(id+"F2.imprint","IMPRINT",EDGE,{"derivedFrom":sQuery(id+"F2.wireOp",EDGE,"E15.0.0")}),1.0]])]})])],"isStart":true}),makeQuery(id+"F5.opExtrude","CAP_FACE",FACE,{"disambiguationData":[OSD([sQuery(id+"F4.wireOp",EDGE,"E16")])],"isStart":true})]});Q0=makeQuery(id+"F7.opBoolean","MERGE",FACE,{"derivedFrom":[subQ0,makeQuery(id+"F6.opPattern","COPY",FACE,{"derivedFrom":subQ0,"instanceName":"1"}),makeQuery(id+"F6.opPattern","COPY",FACE,{"derivedFrom":subQ0,"instanceName":"2"}),makeQuery(id+"F6.opPattern","COPY",FACE,{"derivedFrom":subQ0,"instanceName":"3"}),makeQuery(id+"F6.opPattern","COPY",FACE,{"derivedFrom":subQ0,"instanceName":"4"}),makeQuery(id+"F6.opPattern","COPY",FACE,{"derivedFrom":subQ0,"instanceName":"5"}),makeQuery(id+"F6.opPattern","COPY",FACE,{"derivedFrom":subQ0,"instanceName":"6"}),makeQuery(id+"F6.opPattern","COPY",FACE,{"derivedFrom":subQ0,"instanceName":"7"}),makeQuery(id+"F6.opPattern","COPY",FACE,{"derivedFrom":subQ0,"instanceName":"8"}),makeQuery(id+"F6.opPattern","COPY",FACE,{"derivedFrom":subQ0,"instanceName":"9"}),makeQuery(id+"F6.opPattern","COPY",FACE,{"derivedFrom":subQ0,"instanceName":"10"}),makeQuery(id+"F6.opPattern","COPY",FACE,{"derivedFrom":subQ0,"instanceName":"11"}),makeQuery(id+"F6.opPattern","COPY",FACE,{"derivedFrom":subQ0,"instanceName":"12"}),makeQuery(id+"F6.opPattern","COPY",FACE,{"derivedFrom":subQ0,"instanceName":"13"}),makeQuery(id+"F6.opPattern","COPY",FACE,{"derivedFrom":subQ0,"instanceName":"14"}),makeQuery(id+"F6.opPattern","COPY",FACE,{"derivedFrom":subQ0,"instanceName":"15"}),makeQuery(id+"F6.opPattern","COPY",FACE,{"derivedFrom":subQ0,"instanceName":"16"}),makeQuery(id+"F6.opPattern","COPY",FACE,{"derivedFrom":subQ0,"instanceName":"17"}),makeQuery(id+"F6.opPattern","COPY",FACE,{"derivedFrom":subQ0,"instanceName":"18"}),makeQuery(id+"F6.opPattern","COPY",FACE,{"derivedFrom":subQ0,"instanceName":"19"}),makeQuery(id+"F6.opPattern","COPY",FACE,{"derivedFrom":subQ0,"instanceName":"20"}),makeQuery(id+"F6.opPattern","COPY",FACE,{"derivedFrom":subQ0,"instanceName":"21"}),makeQuery(id+"F6.opPattern","COPY",FACE,{"derivedFrom":subQ0,"instanceName":"22"}),makeQuery(id+"F6.opPattern","COPY",FACE,{"derivedFrom":subQ0,"instanceName":"23"}),makeQuery(id+"F6.opPattern","COPY",FACE,{"derivedFrom":subQ0,"instanceName":"24"}),makeQuery(id+"F6.opPattern","COPY",FACE,{"derivedFrom":subQ0,"instanceName":"25"}),makeQuery(id+"F6.opPattern","COPY",FACE,{"derivedFrom":subQ0,"instanceName":"26"}),makeQuery(id+"F6.opPattern","COPY",FACE,{"derivedFrom":subQ0,"instanceName":"27"}),makeQuery(id+"F6.opPattern","COPY",FACE,{"derivedFrom":subQ0,"instanceName":"28"}),makeQuery(id+"F6.opPattern","COPY",FACE,{"derivedFrom":subQ0,"instanceName":"29"}),makeQuery(id+"F6.opPattern","COPY",FACE,{"derivedFrom":subQ0,"instanceName":"30"}),makeQuery(id+"F6.opPattern","COPY",FACE,{"derivedFrom":subQ0,"instanceName":"31"}),makeQuery(id+"F6.opPattern","COPY",FACE,{"derivedFrom":subQ0,"instanceName":"32"}),makeQuery(id+"F6.opPattern","COPY",FACE,{"derivedFrom":subQ0,"instanceName":"33"}),makeQuery(id+"F6.opPattern","COPY",FACE,{"derivedFrom":subQ0,"instanceName":"34"}),makeQuery(id+"F6.opPattern","COPY",FACE,{"derivedFrom":subQ0,"instanceName":"35"})]});}
            var sketch = newSketch(context, id + "F8", { "sketchPlane" : qUnion([Q0])});
            skCircle(sketch, "E17", {"center": v(0, 0) * mm, "radius": 6.35 * mm});
            skSolve(sketch);
        }
        {
            var Q0;
            Q0 = qSketchRegion(id + "F8", true);
            extrude(context, id + "F9", {"entities" : qUnion([Q0]), "operationType" : NewBodyOperationType.REMOVE, "endBound" : BoundingType.THROUGH_ALL, "oppositeDirection" : true, "depth" : 25.4 * mm});
        }
    });
